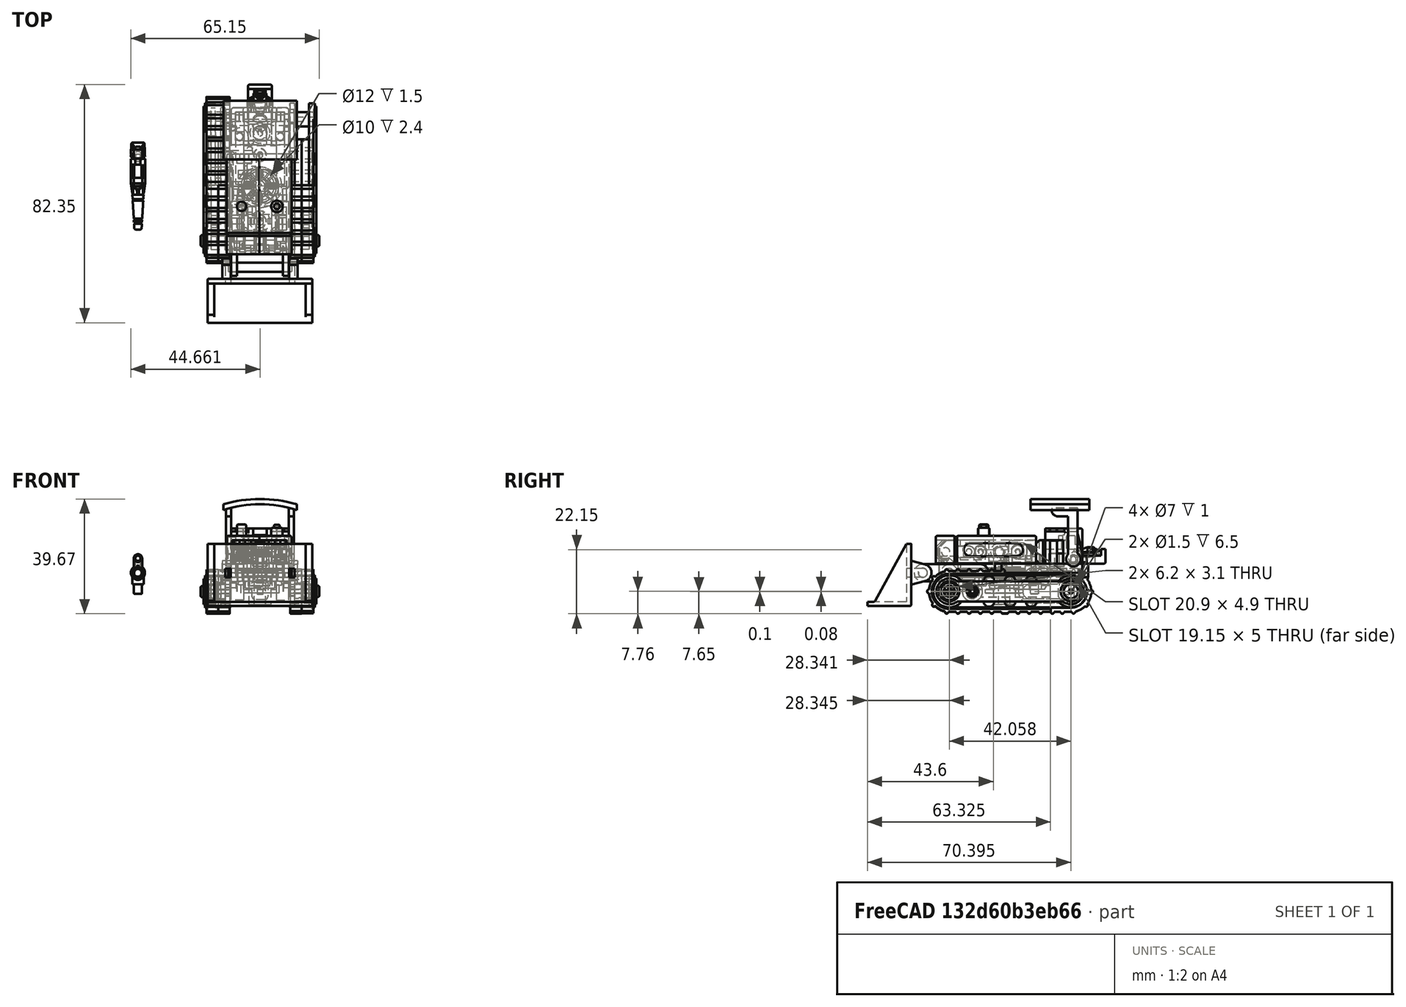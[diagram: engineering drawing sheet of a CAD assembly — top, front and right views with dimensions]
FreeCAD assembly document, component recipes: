
FREECAD ASSEMBLY — COMPONENT RECIPES ("Bonecrusher")

This assembly document has 22 components, labeled P0..P21 below (a component is one placed body or linked part). 22 of them carry a construction recipe — the FreeCAD feature program that regenerates the part from scratch, quoted from this document or its linked companion documents; the rest are supplied as boundary geometry only. No exploded tour is included for this assembly.
NOTE — document 2 of 4 of this assembly tour. The two overview renders and the header above are repeated from document 1; the component sections below continue where the previous document stopped.
COMPONENT P5 — recipe-attached ("L_Arm_Shield", modeled in this document).
Construction recipe (the document's own serialized feature program — sketch geometry with constraints, then the solid features built on it; lengths are millimeters unless a unit is written):

FEATURE [Sketcher::SketchObject] Sketch164
  ArcFitTolerance = 1e-06
  AttachmentSupport = -> [XY_Plane016]
  FullyConstrained = true
  MakeInternals = false
  MapMode = 5
  sketch-geometry (4):
    g0: LineSegment StartX=-34.7 StartY=4.75 StartZ=0 EndX=-34.7 EndY=-4.75 EndZ=0
    g1: LineSegment StartX=-34.7 StartY=-4.75 StartZ=0 EndX=0 EndY=-4.75 EndZ=0
    g2: LineSegment StartX=0 StartY=-4.75 StartZ=0 EndX=0 EndY=4.75 EndZ=0
    g3: LineSegment StartX=0 StartY=4.75 StartZ=0 EndX=-34.7 EndY=4.75 EndZ=0
  constraints (12):
    c: Coincident(g0,g1)
    c: Coincident(g1,g2)
    c: Coincident(g2,g3)
    c: Coincident(g3,g0)
    c: Vertical(g0)
    c: Vertical(g2)
    c: Horizontal(g1)
    c: Horizontal(g3)
    c: PointOnObject(g1,g-2)
    c: DistanceX(g3,g3) = 34.7
    c: DistanceY(g0,g0) = 9.5
    c: DistanceY(g-1,g2) = 4.75
FEATURE [PartDesign::Pad] Pad087
  Direction = (0,0,1)
  Length = 10.2
  Length2 = 10
  Profile = -> Sketch164
  ReferenceAxis = -> Sketch164 [N_Axis]
  Refine = true
  Suppressed = false
  Type = 0
FEATURE [Sketcher::SketchObject] Sketch165
  ArcFitTolerance = 1e-06
  AttachmentSupport = -> [Pad087]
  ExternalGeometry = -> [Pad087]
  FullyConstrained = true
  MakeInternals = false
  MapMode = 5
  Placement = pos=(0,0,10.2) rot=(0,0,1;0rad)
  sketch-geometry (4):
    g0: LineSegment StartX=-34.7 StartY=4.75 StartZ=0 EndX=-34.7 EndY=-3.25 EndZ=0
    g1: LineSegment StartX=-34.7 StartY=-3.25 StartZ=0 EndX=0 EndY=-3.25 EndZ=0
    g2: LineSegment StartX=0 StartY=-3.25 StartZ=0 EndX=0 EndY=4.75 EndZ=0
    g3: LineSegment StartX=0 StartY=4.75 StartZ=0 EndX=-34.7 EndY=4.75 EndZ=0
  constraints (11):
    c: Coincident(g0,g1)
    c: Coincident(g1,g2)
    c: Coincident(g2,g3)
    c: Coincident(g3,g0)
    c: Vertical(g0)
    c: Vertical(g2)
    c: Horizontal(g1)
    c: Horizontal(g3)
    c: Coincident(g0,g-3)
    c: PointOnObject(g1,g-4)
    c: DistanceY(g2,g2) = 8
FEATURE [PartDesign::Pocket] Pocket082
  BaseFeature = -> Pad087
  Direction = (0,0,-1)
  Length = 8.4
  Length2 = 5
  Profile = -> Sketch165
  ReferenceAxis = -> Sketch165 [N_Axis]
  Refine = true
  Suppressed = false
  Type = 0
FEATURE [Sketcher::SketchObject] Sketch166
  ArcFitTolerance = 1e-06
  AttachmentSupport = -> [Pocket082]
  ExternalGeometry = -> [Pocket082]
  FullyConstrained = true
  MakeInternals = false
  MapMode = 5
  Placement = pos=(0,0,1.8) rot=(0,0,1;0rad)
  sketch-geometry (4):
    g0: LineSegment StartX=-18.4 StartY=4.75 StartZ=0 EndX=-18.4 EndY=-3.25 EndZ=0
    g1: LineSegment StartX=-18.4 StartY=-3.25 StartZ=0 EndX=-7.1 EndY=-3.25 EndZ=0
    g2: LineSegment StartX=-7.1 StartY=-3.25 StartZ=0 EndX=-7.1 EndY=4.75 EndZ=0
    g3: LineSegment StartX=-7.1 StartY=4.75 StartZ=0 EndX=-18.4 EndY=4.75 EndZ=0
  constraints (12):
    c: Coincident(g0,g1)
    c: Coincident(g1,g2)
    c: Coincident(g2,g3)
    c: Coincident(g3,g0)
    c: Vertical(g0)
    c: Vertical(g2)
    c: Horizontal(g1)
    c: Horizontal(g3)
    c: DistanceX(g1,g-1) = 7.1
    c: DistanceX(g3,g3) = 11.3
    c: PointOnObject(g2,g-3)
    c: PointOnObject(g1,g-4)
FEATURE [PartDesign::Pad] Pad088
  BaseFeature = -> Pocket082
  Direction = (0,0,1)
  Length = 3.8
  Length2 = 10
  Profile = -> Sketch166
  ReferenceAxis = -> Sketch166 [N_Axis]
  Refine = true
  Suppressed = false
  Type = 0
FEATURE [Sketcher::SketchObject] Sketch167
  ArcFitTolerance = 1e-06
  AttachmentSupport = -> [Pad088]
  ExternalGeometry = -> [Pad088]
  FullyConstrained = true
  MakeInternals = false
  MapMode = 5
  Placement = pos=(0,0,1.8) rot=(0,0,1;0rad)
  sketch-geometry (1):
    g0: Circle CenterX=-22 CenterY=0.75 CenterZ=0 NormalX=0 NormalY=0 NormalZ=1 AngleXU=0 Radius=1.5
  constraints (3):
    c: Diameter(g0) = 3
    c: DistanceX(g-3,g0) = 12.7
    c: DistanceY(g0,g-3) = 4
FEATURE [PartDesign::Pad] Pad089
  BaseFeature = -> Pad088
  Direction = (0,0,1)
  Length = 7.5
  Length2 = 10
  Profile = -> Sketch167
  ReferenceAxis = -> Sketch167 [N_Axis]
  Refine = true
  Suppressed = false
  Type = 0
FEATURE [PartDesign::Fillet] Fillet035
  Base = -> Pad089 [Edge7,Edge2,Edge1,Edge10,Edge8]
  BaseFeature = -> Pad089
  Radius = 0.5
  Refine = true
  SupportTransform = false
  Suppressed = false
  UseAllEdges = false
FEATURE [Sketcher::SketchObject] Sketch168
  ArcFitTolerance = 1e-06
  AttachmentSupport = -> [Fillet035]
  ExternalGeometry = -> [Fillet035]
  FullyConstrained = true
  MakeInternals = false
  MapMode = 5
  Placement = pos=(0,0,5.6) rot=(0,0,1;0rad)
  sketch-geometry (4):
    g0: LineSegment StartX=-17.15 StartY=3.5 StartZ=0 EndX=-17.15 EndY=-3.25 EndZ=0
    g1: LineSegment StartX=-17.15 StartY=-3.25 StartZ=0 EndX=-8.35 EndY=-3.25 EndZ=0
    g2: LineSegment StartX=-8.35 StartY=-3.25 StartZ=0 EndX=-8.35 EndY=3.5 EndZ=0
    g3: LineSegment StartX=-8.35 StartY=3.5 StartZ=0 EndX=-17.15 EndY=3.5 EndZ=0
  constraints (12):
    c: Coincident(g0,g1)
    c: Coincident(g1,g2)
    c: Coincident(g2,g3)
    c: Coincident(g3,g0)
    c: Vertical(g0)
    c: Vertical(g2)
    c: Horizontal(g1)
    c: Horizontal(g3)
    c: DistanceY(g0,g-3) = 1.25
    c: PointOnObject(g0,g-4)
    c: DistanceX(g2,g-3) = 1.25
    c: DistanceX(g-3,g0) = 1.25
FEATURE [PartDesign::Pocket] Pocket083
  BaseFeature = -> Fillet035
  Direction = (0,0,-1)
  Length = 3.81
  Length2 = 5
  Profile = -> Sketch168
  ReferenceAxis = -> Sketch168 [N_Axis]
  Refine = true
  Suppressed = false
  Type = 0
FEATURE [Sketcher::SketchObject] Sketch169
  ArcFitTolerance = 1e-06
  AttachmentSupport = -> [Pocket083]
  ExternalGeometry = -> [Pocket083]
  FullyConstrained = false
  MakeInternals = false
  MapMode = 5
  Placement = pos=(0,0,1.79) rot=(0,0,1;0rad)
  sketch-geometry (4):
    g0: LineSegment StartX=-8.35 StartY=2.75 StartZ=0 EndX=-11.5 EndY=2.75 EndZ=0
    g1: ArcOfCircle CenterX=-11.5 CenterY=0.75 CenterZ=0 NormalX=0 NormalY=0 NormalZ=1 AngleXU=0 Radius=2 StartAngle=1.5708 EndAngle=4.71238
    g2: LineSegment StartX=-11.5 StartY=-1.25 StartZ=0 EndX=-8.35 EndY=-1.25 EndZ=0
    g3: LineSegment StartX=-8.35 StartY=-1.25 StartZ=0 EndX=-8.35 EndY=2.75 EndZ=0
  constraints (12):
    c: Horizontal(g0)
    c: Coincident(g1,g0)
    c: Coincident(g2,g1)
    c: Horizontal(g2)
    c: Coincident(g3,g2)
    c: Coincident(g3,g0)
    c: Vertical(g3)
    c: PointOnObject(g0,g-3)
    c: DistanceY(g2,g0) = 4
    c: DistanceY(g0,g-4) = 2
    c: Diameter(g1) = 4
    c: DistanceX(g0,g0) = 3.15
FEATURE [Sketcher::SketchObject] Sketch170
  ArcFitTolerance = 1e-06
  AttachmentSupport = -> [Pocket083]
  ExternalGeometry = -> [Pocket083]
  FullyConstrained = true
  MakeInternals = false
  MapMode = 5
  Placement = pos=(0,0,5.6) rot=(0,0,1;0rad)
  sketch-geometry (4):
    g0: LineSegment StartX=-8.35 StartY=2.75 StartZ=0 EndX=-8.35 EndY=-1.25 EndZ=0
    g1: LineSegment StartX=-8.35 StartY=-1.25 StartZ=0 EndX=-7.1 EndY=-1.25 EndZ=0
    g2: LineSegment StartX=-7.1 StartY=-1.25 StartZ=0 EndX=-7.1 EndY=2.75 EndZ=0
    g3: LineSegment StartX=-7.1 StartY=2.75 StartZ=0 EndX=-8.35 EndY=2.75 EndZ=0
  constraints (12):
    c: Coincident(g0,g1)
    c: Coincident(g1,g2)
    c: Coincident(g2,g3)
    c: Coincident(g3,g0)
    c: Vertical(g0)
    c: Vertical(g2)
    c: Horizontal(g1)
    c: Horizontal(g3)
    c: DistanceY(g2,g-3) = 2
    c: PointOnObject(g0,g-4)
    c: PointOnObject(g2,g-5)
    c: DistanceY(g1,g2) = 4
FEATURE [PartDesign::Pocket] Pocket084
  BaseFeature = -> Pocket083
  Direction = (0,0,-1)
  Length = 1.25
  Length2 = 5
  Profile = -> Sketch170
  ReferenceAxis = -> Sketch170 [N_Axis]
  Refine = true
  Suppressed = false
  Type = 0
FEATURE [PartDesign::Pad] Pad090
  BaseFeature = -> Pocket084
  Direction = (0,0,1)
  Length = 2.56
  Length2 = 10
  Profile = -> Sketch169
  ReferenceAxis = -> Sketch169 [N_Axis]
  Refine = true
  Suppressed = false
  Type = 0
FEATURE [Sketcher::SketchObject] Sketch171
  ArcFitTolerance = 1e-06
  AttachmentSupport = -> [Pad090]
  ExternalGeometry = -> [Pad090]
  FullyConstrained = true
  MakeInternals = false
  MapMode = 5
  Placement = pos=(0,0,1.79) rot=(0,0,1;0rad)
  sketch-geometry (1):
    g0: Circle CenterX=-15.5 CenterY=0.75 CenterZ=0 NormalX=0 NormalY=0 NormalZ=1 AngleXU=0 Radius=1.9
  constraints (3):
    c: DistanceY(g0,g-3) = 4
    c: Diameter(g0) = 3.8
    c: DistanceX(g-5,g0) = 1.65
FEATURE [PartDesign::Pad] Pad091
  BaseFeature = -> Pad090
  Direction = (0,0,1)
  Length = 5
  Length2 = 10
  Profile = -> Sketch171
  ReferenceAxis = -> Sketch171 [N_Axis]
  Refine = true
  Suppressed = false
  Type = 0
FEATURE [Sketcher::SketchObject] Sketch172
  ArcFitTolerance = 1e-06
  AttachmentSupport = -> [Pad091]
  ExternalGeometry = -> [Pad091]
  FullyConstrained = true
  MakeInternals = false
  MapMode = 5
  Placement = pos=(0,0,4.35) rot=(0,0,1;0rad)
  sketch-geometry (1):
    g0: Circle CenterX=-11.5 CenterY=0.75 CenterZ=0 NormalX=0 NormalY=0 NormalZ=1 AngleXU=0 Radius=1.05
  constraints (3):
    c: DistanceY(g0,g-4) = 2
    c: DistanceX(g0,g-3) = 4.4
    c: Diameter(g0) = 2.1
FEATURE [PartDesign::Pocket] Pocket085
  BaseFeature = -> Pad091
  Direction = (0,0,-1)
  Length = 2.56
  Length2 = 5
  Profile = -> Sketch172
  ReferenceAxis = -> Sketch172 [N_Axis]
  Refine = true
  Suppressed = false
  Type = 0
FEATURE [Sketcher::SketchObject] Sketch173
  ArcFitTolerance = 1e-06
  AttachmentSupport = -> [Pocket085]
  ExternalGeometry = -> [Pocket085]
  FullyConstrained = true
  MakeInternals = false
  MapMode = 5
  Placement = pos=(0,0,6.79) rot=(0,0,1;0rad)
  sketch-geometry (1):
    g0: Circle CenterX=-15.5 CenterY=0.75 CenterZ=0 NormalX=0 NormalY=0 NormalZ=1 AngleXU=0 Radius=0.75
  constraints (2):
    c: Diameter(g0) = 1.5
    c: Coincident(g0,g-3)
FEATURE [PartDesign::Pocket] Pocket086
  BaseFeature = -> Pocket085
  Direction = (0,0,-1)
  Length = 5
  Length2 = 5
  Profile = -> Sketch173
  ReferenceAxis = -> Sketch173 [N_Axis]
  Refine = true
  Suppressed = false
  Type = 0
FEATURE [Sketcher::SketchObject] Sketch174
  ArcFitTolerance = 1e-06
  AttachmentSupport = -> [Pocket086]
  ExternalGeometry = -> [Pocket086]
  FullyConstrained = true
  MakeInternals = false
  MapMode = 5
  Placement = pos=(0,0,0) rot=(1,0,0;3.14159rad)
  sketch-geometry (8):
    g0: ArcOfCircle CenterX=-27.95 CenterY=0 CenterZ=0 NormalX=0 NormalY=0 NormalZ=1 AngleXU=0 Radius=2.25 StartAngle=1.5708 EndAngle=4.71239
    g1: ArcOfCircle CenterX=-11.95 CenterY=1e-16 CenterZ=0 NormalX=0 NormalY=0 NormalZ=1 AngleXU=0 Radius=2.25 StartAngle=4.71239 EndAngle=7.85398
    g2: LineSegment StartX=-27.95 StartY=2.25 StartZ=0 EndX=-11.95 EndY=2.25 EndZ=0
    g3: LineSegment StartX=-27.95 StartY=-2.25 StartZ=0 EndX=-11.95 EndY=-2.25 EndZ=0
    g4: LineSegment StartX=-7.45 StartY=4.75 StartZ=0 EndX=-7.45 EndY=-4.75 EndZ=0
    g5: LineSegment StartX=-7.45 StartY=-4.75 StartZ=0 EndX=-6.45 EndY=-4.75 EndZ=0
    g6: LineSegment StartX=-6.45 StartY=-4.75 StartZ=0 EndX=-6.45 EndY=4.75 EndZ=0
    g7: LineSegment StartX=-6.45 StartY=4.75 StartZ=0 EndX=-7.45 EndY=4.75 EndZ=0
  constraints (22):
    c: Tangent(g0,g2) = 1.5708
    c: Tangent(g0,g3) = -1.5708
    c: Tangent(g1,g2) = 1.5708
    c: Tangent(g1,g3) = -1.5708
    c: Equal(g0,g1)
    c: Horizontal(g3)
    c: PointOnObject(g0,g-1)
    c: Diameter(g0) = 4.5
    c: DistanceX(g-3,g0) = 6.75
    c: DistanceX(g0,g1) = 16
    c: Coincident(g4,g5)
    c: Coincident(g5,g6)
    c: Coincident(g6,g7)
    c: Coincident(g7,g4)
    c: Vertical(g4)
    c: Vertical(g6)
    c: Horizontal(g5)
    c: Horizontal(g7)
    c: PointOnObject(g6,g-4)
    c: PointOnObject(g5,g-5)
    c: DistanceX(g1,g4) = 4.5
    c: DistanceX(g4,g6) = 1
FEATURE [PartDesign::Pocket] Pocket087
  BaseFeature = -> Pocket086
  Direction = (0,0,1)
  Length = 0.3
  Length2 = 5
  Profile = -> Sketch174
  ReferenceAxis = -> Sketch174 [N_Axis]
  Refine = true
  Suppressed = false
  Type = 0
FEATURE [Sketcher::SketchObject] Sketch175
  ArcFitTolerance = 1e-06
  AttachmentSupport = -> [Pocket087]
  ExternalGeometry = -> [Pocket087]
  FullyConstrained = true
  MakeInternals = false
  MapMode = 5
  Placement = pos=(0,-4.75,0) rot=(1,0,0;1.5708rad)
  sketch-geometry (4):
    g0: LineSegment StartX=-7.45 StartY=10.2 StartZ=0 EndX=-7.45 EndY=0 EndZ=0
    g1: LineSegment StartX=-7.45 StartY=0 StartZ=0 EndX=-6.45 EndY=0 EndZ=0
    g2: LineSegment StartX=-6.45 StartY=0 StartZ=0 EndX=-6.45 EndY=10.2 EndZ=0
    g3: LineSegment StartX=-6.45 StartY=10.2 StartZ=0 EndX=-7.45 EndY=10.2 EndZ=0
  constraints (11):
    c: Coincident(g0,g1)
    c: Coincident(g1,g2)
    c: Coincident(g2,g3)
    c: Coincident(g3,g0)
    c: Vertical(g0)
    c: Vertical(g2)
    c: Horizontal(g1)
    c: Horizontal(g3)
    c: DistanceX(g3,g3) = 1
    c: Coincident(g0,g-3)
    c: PointOnObject(g0,g-4)
FEATURE [PartDesign::Pocket] Pocket088
  BaseFeature = -> Pocket087
  Direction = (0,1,-2e-16)
  Length = 0.3
  Length2 = 5
  Profile = -> Sketch175
  ReferenceAxis = -> Sketch175 [N_Axis]
  Refine = true
  Suppressed = false
  Type = 0
FEATURE [PartDesign::Fillet] Fillet036
  Base = -> Pocket088 [Edge90,Edge91,Edge89,Edge92]
  BaseFeature = -> Pocket088
  Radius = 0.2
  Refine = true
  SupportTransform = false
  Suppressed = false
  UseAllEdges = false
FEATURE [PartDesign::Fillet] Fillet037
  Base = -> Fillet036 [Edge5,Edge94,Edge20,Edge19,Edge18,Edge17,Edge93,Edge97,Edge96,Edge95]
  BaseFeature = -> Fillet036
  Radius = 0.2
  Refine = true
  SupportTransform = false
  Suppressed = false
  UseAllEdges = false
FEATURE [Sketcher::SketchObject] Sketch176
  ArcFitTolerance = 1e-06
  AttachmentSupport = -> [Fillet037]
  ExternalGeometry = -> [Fillet037]
  FullyConstrained = true
  MakeInternals = false
  MapMode = 5
  Placement = pos=(0,-4.75,0) rot=(1,0,0;1.5708rad)
  sketch-geometry (1):
    g0: Circle CenterX=-16.6 CenterY=5.1 CenterZ=0 NormalX=0 NormalY=0 NormalZ=1 AngleXU=0 Radius=2
  constraints (3):
    c: Diameter(g0) = 4
    c: DistanceY(g0,g-3) = 5.1
    c: DistanceX(g0,g-4) = 16.6
FEATURE [PartDesign::Pad] Pad092
  BaseFeature = -> Fillet037
  Direction = (0,-1,2e-16)
  Length = 2.8
  Length2 = 10
  Profile = -> Sketch176
  ReferenceAxis = -> Sketch176 [N_Axis]
  Refine = true
  Suppressed = false
  Type = 0
FEATURE [PartDesign::Fillet] Fillet038
  Base = -> Pad092 [Edge116]
  BaseFeature = -> Pad092
  Radius = 0.5
  Refine = true
  SupportTransform = false
  Suppressed = false
  UseAllEdges = false
FEATURE [PartDesign::Fillet] Fillet039
  Base = -> Fillet038 [Edge89,Edge85]
  BaseFeature = -> Fillet038
  Radius = 0.5
  Refine = true
  SupportTransform = false
  Suppressed = false
  UseAllEdges = false
FEATURE [Sketcher::SketchObject] Sketch178
  ArcFitTolerance = 1e-06
  AttachmentSupport = -> [Fillet039]
  ExternalGeometry = -> [Fillet039]
  FullyConstrained = true
  MakeInternals = false
  MapMode = 5
  Placement = pos=(0,-7.55,2e-15) rot=(1,0,0;1.5708rad)
  sketch-geometry (1):
    g0: Circle CenterX=-16.6 CenterY=5.1 CenterZ=0 NormalX=0 NormalY=0 NormalZ=1 AngleXU=0 Radius=1
  constraints (2):
    c: Coincident(g0,g-3)
    c: Diameter(g0) = 2
FEATURE [PartDesign::Pad] Pad093
  BaseFeature = -> Fillet039
  Direction = (0,-1,2e-16)
  Length = 1.1
  Length2 = 10
  Profile = -> Sketch178
  ReferenceAxis = -> Sketch178 [N_Axis]
  Refine = true
  Suppressed = false
  Type = 0
FEATURE [PartDesign::Fillet] Fillet040
  Base = -> Pad093 [Edge182]
  BaseFeature = -> Pad093
  Radius = 0.5
  Refine = true
  SupportTransform = false
  Suppressed = false
  UseAllEdges = false
FEATURE [Sketcher::SketchObject] Sketch283
  ArcFitTolerance = 1e-06
  AttachmentSupport = -> [Fillet040]
  ExternalGeometry = -> [Fillet040]
  FullyConstrained = true
  MakeInternals = false
  MapMode = 5
  Placement = pos=(0,0,10.2) rot=(0,0,1;0rad)
  sketch-geometry (12):
    g0: LineSegment StartX=0 StartY=-3.25 StartZ=0 EndX=1e-16 EndY=-4.25 EndZ=0
    g1: LineSegment StartX=-0.5 StartY=-4.75 StartZ=0 EndX=-6.25 EndY=-4.75 EndZ=0
    g2: ArcOfCircle CenterX=-6.25 CenterY=-4.55 CenterZ=0 NormalX=0 NormalY=0 NormalZ=1 AngleXU=0 Radius=0.2 StartAngle=3.14159 EndAngle=4.71239
    g3: LineSegment StartX=-6.45 StartY=-4.55 StartZ=0 EndX=-6.45 EndY=-4.45 EndZ=0
    g4: LineSegment StartX=-6.45 StartY=-4.45 StartZ=0 EndX=-7.45 EndY=-4.45 EndZ=0
    g5: LineSegment StartX=-7.45 StartY=-4.45 StartZ=0 EndX=-7.45 EndY=-4.55 EndZ=0
    g6: ArcOfCircle CenterX=-7.65 CenterY=-4.55 CenterZ=0 NormalX=0 NormalY=0 NormalZ=1 AngleXU=0 Radius=0.2 StartAngle=4.71239 EndAngle=6.28319
    g7: LineSegment StartX=-7.65 StartY=-4.75 StartZ=0 EndX=-34.2 EndY=-4.75 EndZ=0
    g8: ArcOfCircle CenterX=-34.2 CenterY=-4.25 CenterZ=0 NormalX=0 NormalY=0 NormalZ=1 AngleXU=0 Radius=0.5 StartAngle=3.14159 EndAngle=4.71239
    g9: LineSegment StartX=-34.7 StartY=-4.25 StartZ=0 EndX=-34.7 EndY=-3.25 EndZ=0
    g10: LineSegment StartX=-34.7 StartY=-3.25 StartZ=0 EndX=0 EndY=-3.25 EndZ=0
    g11: ArcOfCircle CenterX=-0.5 CenterY=-4.25 CenterZ=0 NormalX=0 NormalY=0 NormalZ=1 AngleXU=0 Radius=0.5 StartAngle=4.71239 EndAngle=6.28319
  constraints (28):
    c: Coincident(g2,g-9)
    c: Coincident(g2,g1)
    c: Coincident(g4,g3)
    c: Coincident(g4,g-10)
    c: Coincident(g5,g4)
    c: Coincident(g5,g-11)
    c: Coincident(g6,g5)
    c: Coincident(g6,g-12)
    c: Coincident(g8,g7)
    c: Coincident(g8,g-14)
    c: Coincident(g10,g9)
    c: Coincident(g10,g0)
    c: Coincident(g0,g-5)
    c: Coincident(g1,g-6)
    c: Coincident(g0,g-4)
    c: Coincident(g1,g-7)
    c: Coincident(g3,g2)
    c: Radius(g2) = 0.2
    c: Coincident(g3,g-9)
    c: Coincident(g11,g0)
    c: Coincident(g11,g1)
    c: Radius(g11) = 0.5
    c: Coincident(g7,g6)
    c: Radius(g6) = 0.2
    c: Coincident(g9,g8)
    c: Coincident(g-13,g7)
    c: Radius(g8) = 0.5
    c: Coincident(g9,g-14)
FEATURE [PartDesign::Pad] Pad162
  BaseFeature = -> Fillet040
  Direction = (0,0,1)
  Length = 1
  Length2 = 10
  Profile = -> Sketch283
  ReferenceAxis = -> Sketch283 [N_Axis]
  Refine = true
  Suppressed = false
  Type = 0
FEATURE [PartDesign::Body] Body014  label="L_Arm_Shield"
  AllowCompound = false
  Group = -> [Sketch164,Pad087,Sketch165,Pocket082,Sketch166,Pad088,Sketch167,Pad089,Fillet035,Sketch168,Pocket083,Sketch169,Sketch170,Pocket084,Pad090,Sketch171,Pad091,Sketch172,Pocket085,Sketch173,Pocket086,Sketch174,Pocket087,Sketch175,Pocket088,Fillet036,Fillet037,Sketch176,Pad092,Fillet038,Fillet039,Sketch178,Pad093,Fillet040,Sketch283,Pad162]
  Origin = -> Origin016
  Tip = -> Pad162
COMPONENT P6 — recipe-attached ("Right_Inner_Leg", modeled in this document).
Construction recipe (the document's own serialized feature program — sketch geometry with constraints, then the solid features built on it; lengths are millimeters unless a unit is written):

FEATURE [Sketcher::SketchObject] Sketch187
  ArcFitTolerance = 1e-06
  AttachmentSupport = -> [XY_Plane017]
  FullyConstrained = true
  MakeInternals = false
  MapMode = 5
  sketch-geometry (4):
    g0: LineSegment StartX=3e-16 StartY=5.55 StartZ=0 EndX=42.05 EndY=5.55 EndZ=0
    g1: ArcOfCircle CenterX=42.05 CenterY=3.35631e-11 CenterZ=0 NormalX=0 NormalY=0 NormalZ=1 AngleXU=0 Radius=5.55 StartAngle=4.71239 EndAngle=7.85398
    g2: LineSegment StartX=42.05 StartY=-5.55 StartZ=0 EndX=0 EndY=-5.55 EndZ=0
    g3: ArcOfCircle CenterX=0 CenterY=0 CenterZ=0 NormalX=0 NormalY=0 NormalZ=1 AngleXU=0 Radius=5.55 StartAngle=1.5708 EndAngle=4.71239
  constraints (13):
    c: PointOnObject(g0,g-2)
    c: Horizontal(g0)
    c: Coincident(g1,g0)
    c: Coincident(g2,g1)
    c: PointOnObject(g2,g-2)
    c: Horizontal(g2)
    c: Coincident(g3,g2)
    c: Coincident(g3,g0)
    c: DistanceX(g0,g0) = 42.05
    c: Radius(g3) = 5.55
    c: Radius(g1) = 5.55
    c: Coincident(g3,g-1)
    c: PointOnObject(g1,g-1)
FEATURE [PartDesign::Pad] Pad098
  Direction = (0,0,1)
  Length = 1.6
  Length2 = 10
  Profile = -> Sketch187
  ReferenceAxis = -> Sketch187 [N_Axis]
  Refine = true
  Suppressed = false
  Type = 0
FEATURE [Sketcher::SketchObject] Sketch188
  ArcFitTolerance = 1e-06
  AttachmentSupport = -> [Pad098]
  ExternalGeometry = -> [Pad098]
  FullyConstrained = true
  MakeInternals = false
  MapMode = 5
  Placement = pos=(0,0,0) rot=(1,0,0;3.14159rad)
  sketch-geometry (8):
    g0: LineSegment StartX=19.17 StartY=5.55 StartZ=0 EndX=0 EndY=5.55 EndZ=0
    g1: ArcOfCircle CenterX=0 CenterY=1e-16 CenterZ=0 NormalX=0 NormalY=0 NormalZ=1 AngleXU=0 Radius=5.55 StartAngle=1.5708 EndAngle=4.71239
    g2: LineSegment StartX=-1e-15 StartY=-5.55 StartZ=0 EndX=35.05 EndY=-5.55 EndZ=0
    g3: LineSegment StartX=19.17 StartY=5.55 StartZ=0 EndX=19.17 EndY=7.05 EndZ=0
    g4: LineSegment StartX=19.17 StartY=7.05 StartZ=0 EndX=0 EndY=7.05 EndZ=0
    g5: ArcOfCircle CenterX=0 CenterY=1e-16 CenterZ=0 NormalX=0 NormalY=0 NormalZ=1 AngleXU=0 Radius=7.05 StartAngle=1.5708 EndAngle=4.71239
    g6: LineSegment StartX=0 StartY=-7.05 StartZ=0 EndX=35.05 EndY=-7.05 EndZ=0
    g7: LineSegment StartX=35.05 StartY=-5.55 StartZ=0 EndX=35.05 EndY=-7.05 EndZ=0
  constraints (24):
    c: Coincident(g0,g-4)
    c: Coincident(g1,g0)
    c: Coincident(g1,g-5)
    c: Coincident(g2,g1)
    c: PointOnObject(g2,g-5)
    c: PointOnObject(g0,g-3)
    c: DistanceX(g2,g2) = 35.05
    c: DistanceX(g0,g0) = 19.17
    c: Coincident(g1,g-1)
    c: Coincident(g3,g0)
    c: Vertical(g3)
    c: Coincident(g4,g3)
    c: PointOnObject(g4,g-2)
    c: Horizontal(g4)
    c: Coincident(g5,g4)
    c: PointOnObject(g5,g-2)
    c: Coincident(g6,g5)
    c: Horizontal(g6)
    c: Coincident(g7,g2)
    c: Coincident(g7,g6)
    c: Vertical(g7)
    c: DistanceY(g3,g3) = 1.5
    c: DistanceY(g7,g7) = 1.5
    c: Coincident(g5,g1)
FEATURE [PartDesign::Pad] Pad099
  BaseFeature = -> Pad098
  Direction = (0,0,-1)
  Length = 4.05
  Length2 = 10
  Profile = -> Sketch188
  ReferenceAxis = -> Sketch188 [N_Axis]
  Refine = true
  Reversed = true
  Suppressed = false
  Type = 0
FEATURE [PartDesign::Pocket] Pocket093
  BaseFeature = -> Pad099
  Direction = (0,0,1)
  Length = 0.1
  Length2 = 5
  Profile = -> Sketch188
  ReferenceAxis = -> Sketch188 [N_Axis]
  Refine = true
  Suppressed = false
  Type = 0
FEATURE [Sketcher::SketchObject] Sketch189
  ArcFitTolerance = 1e-06
  AttachmentSupport = -> [Pocket093]
  FullyConstrained = true
  MakeInternals = false
  MapMode = 5
  Placement = pos=(0,0,0) rot=(1,0,0;3.14159rad)
  sketch-geometry (5):
    g0: LineSegment StartX=-3 StartY=1.5 StartZ=0 EndX=-3 EndY=-1.5 EndZ=0
    g1: LineSegment StartX=-3 StartY=-1.5 StartZ=0 EndX=3 EndY=-1.5 EndZ=0
    g2: LineSegment StartX=3 StartY=-1.5 StartZ=0 EndX=3 EndY=1.5 EndZ=0
    g3: LineSegment StartX=3 StartY=1.5 StartZ=0 EndX=-3 EndY=1.5 EndZ=0
    g4: Circle CenterX=8 CenterY=0 CenterZ=0 NormalX=0 NormalY=0 NormalZ=1 AngleXU=0 Radius=0.75
  constraints (15):
    c: Coincident(g0,g1)
    c: Coincident(g1,g2)
    c: Coincident(g2,g3)
    c: Coincident(g3,g0)
    c: Vertical(g0)
    c: Vertical(g2)
    c: Horizontal(g1)
    c: Horizontal(g3)
    c: DistanceY(g-1,g0) = 1.5
    c: DistanceY(g0,g-1) = 1.5
    c: DistanceX(g0,g-1) = 3
    c: DistanceX(g-1,g2) = 3
    c: PointOnObject(g4,g-1)
    c: Diameter(g4) = 1.5
    c: DistanceX(g-1,g4) = 8
FEATURE [PartDesign::Pocket] Pocket094
  BaseFeature = -> Pocket093
  Direction = (0,0,1)
  Length = 1.6
  Length2 = 5
  Profile = -> Sketch189
  ReferenceAxis = -> Sketch189 [N_Axis]
  Refine = true
  Suppressed = false
  Type = 0
FEATURE [Sketcher::SketchObject] Sketch190
  ArcFitTolerance = 1e-06
  AttachmentSupport = -> [Pocket094]
  ExternalGeometry = -> [Pocket094]
  FullyConstrained = true
  MakeInternals = false
  MapMode = 5
  Placement = pos=(0,0,0.1) rot=(1,0,0;3.14159rad)
  sketch-geometry (38):
    g0: ArcOfCircle CenterX=18.57 CenterY=7.05 CenterZ=0 NormalX=0 NormalY=0 NormalZ=1 AngleXU=0 Radius=0.6 StartAngle=-4.4e-15 EndAngle=3.14159
    g1: ArcOfCircle CenterX=14.67 CenterY=7.05 CenterZ=0 NormalX=0 NormalY=0 NormalZ=1 AngleXU=0 Radius=0.6 StartAngle=-8e-15 EndAngle=3.14159
    g2: ArcOfCircle CenterX=10.77 CenterY=7.05 CenterZ=0 NormalX=0 NormalY=0 NormalZ=1 AngleXU=0 Radius=0.6 StartAngle=6e-16 EndAngle=3.14159
    g3: ArcOfCircle CenterX=6.87 CenterY=7.05 CenterZ=0 NormalX=0 NormalY=0 NormalZ=1 AngleXU=0 Radius=0.6 StartAngle=-4.4e-15 EndAngle=3.14159
    g4: LineSegment StartX=19.17 StartY=7.05 StartZ=0 EndX=17.97 EndY=7.05 EndZ=0
    g5: LineSegment StartX=15.27 StartY=7.05 StartZ=0 EndX=14.07 EndY=7.05 EndZ=0
    g6: LineSegment StartX=11.37 StartY=7.05 StartZ=0 EndX=10.17 EndY=7.05 EndZ=0
    g7: LineSegment StartX=7.47 StartY=7.05 StartZ=0 EndX=6.27 EndY=7.05 EndZ=0
    g8: ArcOfCircle CenterX=2.97 CenterY=7.05 CenterZ=0 NormalX=0 NormalY=0 NormalZ=1 AngleXU=0 Radius=0.6 StartAngle=-1.8e-15 EndAngle=3.14159
    g9: LineSegment StartX=3.57 StartY=7.05 StartZ=0 EndX=2.37 EndY=7.05 EndZ=0
    g10: ArcOfCircle CenterX=-0.927604 CenterY=6.98871 CenterZ=0 NormalX=0 NormalY=0 NormalZ=1 AngleXU=0 Radius=0.6 StartAngle=0.0893917 EndAngle=3.31612
    g11: ArcOfCircle CenterX=-5.30424 CenterY=4.64408 CenterZ=0 NormalX=0 NormalY=0 NormalZ=1 AngleXU=0 Radius=0.6 StartAngle=0.809094 EndAngle=4.03582
    g12: ArcOfCircle CenterX=-7.05 CenterY=0 CenterZ=0 NormalX=0 NormalY=0 NormalZ=1 AngleXU=0 Radius=0.6 StartAngle=1.52823 EndAngle=4.75496
    g13: LineSegment StartX=-7.02447 StartY=0.599457 StartZ=0 EndX=-7.02447 EndY=-0.599457 EndZ=0
    g14: LineSegment StartX=-0.33 StartY=7.04227 StartZ=0 EndX=-1.51849 EndY=6.88453 EndZ=0
    g15: ArcOfCircle CenterX=-5.28202 CenterY=-4.63063 CenterZ=0 NormalX=0 NormalY=0 NormalZ=1 AngleXU=0 Radius=0.6 StartAngle=2.29058 EndAngle=5.43217
    g16: ArcOfCircle CenterX=-0.922566 CenterY=-6.98938 CenterZ=0 NormalX=0 NormalY=0 NormalZ=1 AngleXU=0 Radius=0.6 StartAngle=2.96779 EndAngle=6.19451
    g17: ArcOfCircle CenterX=2.97508 CenterY=-7.05 CenterZ=0 NormalX=0 NormalY=0 NormalZ=1 AngleXU=0 Radius=0.6 StartAngle=3.14159 EndAngle=6.28319
    g18: ArcOfCircle CenterX=6.87508 CenterY=-7.05 CenterZ=0 NormalX=0 NormalY=0 NormalZ=1 AngleXU=0 Radius=0.6 StartAngle=3.14159 EndAngle=6.28319
    g19: ArcOfCircle CenterX=10.7751 CenterY=-7.05 CenterZ=0 NormalX=0 NormalY=0 NormalZ=1 AngleXU=0 Radius=0.6 StartAngle=3.14159 EndAngle=6.28319
    g20: ArcOfCircle CenterX=14.6751 CenterY=-7.05 CenterZ=0 NormalX=0 NormalY=0 NormalZ=1 AngleXU=0 Radius=0.6 StartAngle=3.14159 EndAngle=6.28319
    g21: ArcOfCircle CenterX=23.7751 CenterY=-7.05 CenterZ=0 NormalX=0 NormalY=0 NormalZ=1 AngleXU=0 Radius=0.6 StartAngle=3.14159 EndAngle=6.28319
    g22: ArcOfCircle CenterX=27.6751 CenterY=-7.05 CenterZ=0 NormalX=0 NormalY=0 NormalZ=1 AngleXU=0 Radius=0.6 StartAngle=3.14159 EndAngle=6.28319
    g23: ArcOfCircle CenterX=31.5751 CenterY=-7.05 CenterZ=0 NormalX=0 NormalY=0 NormalZ=1 AngleXU=0 Radius=0.6 StartAngle=3.14159 EndAngle=6.28319
    g24: ArcOfCircle CenterX=18.5751 CenterY=-7.05 CenterZ=0 NormalX=0 NormalY=0 NormalZ=1 AngleXU=0 Radius=0.6 StartAngle=3.14159 EndAngle=4.71239
    g25: ArcOfCircle CenterX=19.8751 CenterY=-7.05 CenterZ=0 NormalX=0 NormalY=0 NormalZ=1 AngleXU=0 Radius=0.6 StartAngle=4.71239 EndAngle=6.28319
    g26: LineSegment StartX=19.8751 StartY=-7.65 StartZ=0 EndX=18.5751 EndY=-7.65 EndZ=0
    g27: LineSegment StartX=20.4751 StartY=-7.05 StartZ=0 EndX=17.9751 EndY=-7.05 EndZ=0
    g28: LineSegment StartX=24.3751 StartY=-7.05 StartZ=0 EndX=23.1751 EndY=-7.05 EndZ=0
    g29: LineSegment StartX=28.2751 StartY=-7.05 StartZ=0 EndX=27.0751 EndY=-7.05 EndZ=0
    g30: LineSegment StartX=32.1751 StartY=-7.05 StartZ=0 EndX=30.9751 EndY=-7.05 EndZ=0
    g31: LineSegment StartX=15.2751 StartY=-7.05 StartZ=0 EndX=14.0751 EndY=-7.05 EndZ=0
    g32: LineSegment StartX=11.3751 StartY=-7.05 StartZ=0 EndX=10.1751 EndY=-7.05 EndZ=0
    g33: LineSegment StartX=7.47508 StartY=-7.05 StartZ=0 EndX=6.27508 EndY=-7.05 EndZ=0
    g34: LineSegment StartX=3.57508 StartY=-7.05 StartZ=0 EndX=2.37508 EndY=-7.05 EndZ=0
    g35: LineSegment StartX=-0.324923 StartY=-7.04251 StartZ=0 EndX=-1.51353 EndY=-6.88562 EndZ=0
    g36: LineSegment StartX=-4.88649 StartY=-5.0818 StartZ=0 EndX=-5.67755 EndY=-4.17946 EndZ=0
    g37: LineSegment StartX=-4.89015 StartY=5.07828 StartZ=0 EndX=-5.67992 EndY=4.17625 EndZ=0
  constraints (132):
    c: Coincident(g4,g0)
    c: Coincident(g4,g0)
    c: Horizontal(g4)
    c: Coincident(g5,g1)
    c: Coincident(g5,g1)
    c: Horizontal(g5)
    c: Coincident(g6,g2)
    c: Coincident(g6,g2)
    c: Horizontal(g6)
    c: Coincident(g7,g3)
    c: Coincident(g7,g3)
    c: Horizontal(g7)
    c: Coincident(g9,g8)
    c: Coincident(g9,g8)
    c: Horizontal(g9)
    c: Radius(g0) = 0.6
    c: Radius(g1) = 0.6
    c: Radius(g2) = 0.6
    c: Radius(g3) = 0.6
    c: DistanceX(g3,g2) = 2.7
    c: Coincident(g0,g-3)
    c: PointOnObject(g0,g4)
    c: PointOnObject(g1,g-4)
    c: PointOnObject(g1,g5)
    c: DistanceX(g1,g0) = 2.7
    c: DistanceX(g2,g1) = 2.7
    c: DistanceX(g8,g3) = 2.7
    c: PointOnObject(g2,g6)
    c: PointOnObject(g2,g-4)
    c: PointOnObject(g3,g-4)
    c: PointOnObject(g3,g7)
    c: PointOnObject(g8,g-4)
    c: PointOnObject(g8,g9)
    c: Radius(g8) = 0.6
    c: PointOnObject(g10,g-5)
    c: PointOnObject(g10,g-5)
    c: PointOnObject(g11,g-5)
    c: PointOnObject(g11,g-5)
    c: PointOnObject(g12,g-5)
    c: PointOnObject(g12,g-5)
    c: PointOnObject(g12,g-1)
    c: PointOnObject(g12,g-5)
    c: Radius(g12) = 0.6
    c: Coincident(g13,g12)
    c: Coincident(g13,g12)
    c: Coincident(g14,g10)
    c: Coincident(g14,g10)
    c: PointOnObject(g15,g-5)
    c: PointOnObject(g15,g-5)
    c: PointOnObject(g16,g-5)
    c: PointOnObject(g16,g-5)
    c: Coincident(g26,g25)
    c: Coincident(g26,g24)
    c: Horizontal(g26)
    c: Coincident(g27,g25)
    c: Coincident(g27,g24)
    c: Horizontal(g27)
    c: Coincident(g28,g21)
    c: Coincident(g28,g21)
    c: Horizontal(g28)
    c: Coincident(g29,g22)
    c: Coincident(g29,g22)
    c: Horizontal(g29)
    c: Coincident(g30,g23)
    c: Coincident(g30,g23)
    c: Horizontal(g30)
    c: Coincident(g31,g20)
    c: Coincident(g31,g20)
    c: Horizontal(g31)
    c: Coincident(g32,g19)
    c: Coincident(g32,g19)
    c: Horizontal(g32)
    c: Coincident(g33,g18)
    c: Coincident(g33,g18)
    c: Horizontal(g33)
    c: Coincident(g34,g17)
    c: Coincident(g34,g17)
    c: Horizontal(g34)
    c: Coincident(g35,g16)
    c: Coincident(g35,g16)
    c: Coincident(g36,g15)
    c: Coincident(g36,g15)
    c: Coincident(g37,g11)
    c: Coincident(g37,g11)
    c: DistanceX(g10,g8) = 2.7
    c: PointOnObject(g10,g-5)
    c: Radius(g10) = 0.6
    c: Radius(g11) = 0.6
    c: Radius(g15) = 0.6
    c: Radius(g16) = 0.6
    c: Radius(g17) = 0.6
    c: Radius(g18) = 0.6
    c: Radius(g19) = 0.6
    c: Radius(g20) = 0.6
    c: Radius(g24) = 0.6
    c: Radius(g25) = 0.6
    c: Radius(g21) = 0.6
    c: Radius(g22) = 0.6
    c: Radius(g23) = 0.6
    c: Distance(g10,g11) = 3.825
    c: PointOnObject(g11,g-5)
    c: PointOnObject(g15,g36)
    c: PointOnObject(g16,g-5)
    c: PointOnObject(g17,g34)
    c: PointOnObject(g17,g-6)
    c: Distance(g12,g15) = 3.825
    c: Distance(g15,g16) = 3.825
    c: DistanceX(g16,g17) = 2.7
    c: DistanceX(g17,g18) = 2.7
    c: DistanceX(g18,g19) = 2.7
    c: DistanceX(g19,g20) = 2.7
    c: DistanceX(g20,g24) = 2.7
    c: DistanceX(g25,g21) = 2.7
    c: DistanceX(g21,g22) = 2.7
    c: DistanceX(g22,g23) = 2.7
    c: PointOnObject(g18,g33)
    c: PointOnObject(g18,g-6)
    c: PointOnObject(g19,g-6)
    c: PointOnObject(g19,g32)
    c: PointOnObject(g20,g31)
    c: PointOnObject(g20,g-6)
    c: PointOnObject(g24,g-6)
    c: DistanceX(g27,g27) = 2.5
    c: PointOnObject(g24,g27)
    c: DistanceX(g25,g25) = 0
    c: DistanceX(g24,g24) = 0
    c: PointOnObject(g21,g28)
    c: PointOnObject(g21,g-6)
    c: PointOnObject(g22,g29)
    c: PointOnObject(g22,g-6)
    c: PointOnObject(g23,g30)
    c: PointOnObject(g23,g-6)
FEATURE [PartDesign::Pad] Pad100
  BaseFeature = -> Pocket094
  Direction = (0,0,-1)
  Length = 3.95
  Length2 = 10
  Profile = -> Sketch190
  ReferenceAxis = -> Sketch190 [N_Axis]
  Refine = true
  Reversed = true
  Suppressed = false
  Type = 0
FEATURE [Sketcher::SketchObject] Sketch191
  ArcFitTolerance = 1e-06
  AttachmentSupport = -> [Pad100]
  ExternalGeometry = -> [Pad100]
  FullyConstrained = true
  MakeInternals = false
  MapMode = 5
  Placement = pos=(0,0,1.6) rot=(0,0,1;0rad)
  sketch-geometry (1):
    g0: Circle CenterX=8 CenterY=0 CenterZ=0 NormalX=0 NormalY=0 NormalZ=1 AngleXU=0 Radius=2.25
  constraints (2):
    c: Coincident(g0,g-3)
    c: Diameter(g0) = 4.5
FEATURE [PartDesign::Pad] Pad101
  BaseFeature = -> Pad100
  Direction = (0,0,1)
  Length = 4.9
  Length2 = 10
  Profile = -> Sketch191
  ReferenceAxis = -> Sketch191 [N_Axis]
  Refine = true
  Suppressed = false
  Type = 0
FEATURE [Sketcher::SketchObject] Sketch192
  ArcFitTolerance = 1e-06
  AttachmentSupport = -> [Pad101]
  ExternalGeometry = -> [Pad101]
  FullyConstrained = true
  MakeInternals = false
  MapMode = 5
  Placement = pos=(0,0,6.5) rot=(0,0,1;0rad)
  sketch-geometry (1):
    g0: Circle CenterX=8 CenterY=0 CenterZ=0 NormalX=0 NormalY=0 NormalZ=1 AngleXU=0 Radius=0.75
  constraints (2):
    c: Coincident(g0,g-3)
    c: Diameter(g0) = 1.5
FEATURE [PartDesign::Pocket] Pocket095
  BaseFeature = -> Pad101
  Direction = (0,0,-1)
  Length = 4.9
  Length2 = 5
  Profile = -> Sketch192
  ReferenceAxis = -> Sketch192 [N_Axis]
  Refine = true
  Suppressed = false
  Type = 0
FEATURE [Sketcher::SketchObject] Sketch193
  ArcFitTolerance = 1e-06
  AttachmentSupport = -> [Pocket095]
  ExternalGeometry = -> [Pocket095]
  FullyConstrained = true
  MakeInternals = false
  MapMode = 5
  Placement = pos=(0,0,1.6) rot=(0,0,1;0rad)
  sketch-geometry (1):
    g0: Circle CenterX=42.05 CenterY=0 CenterZ=0 NormalX=0 NormalY=0 NormalZ=1 AngleXU=0 Radius=2.475
  constraints (2):
    c: Coincident(g0,g-3)
    c: Diameter(g0) = 4.95
FEATURE [PartDesign::Pad] Pad102
  BaseFeature = -> Pocket095
  Direction = (0,0,1)
  Length = 6.5
  Length2 = 10
  Profile = -> Sketch193
  ReferenceAxis = -> Sketch193 [N_Axis]
  Refine = true
  Suppressed = false
  Type = 0
FEATURE [Sketcher::SketchObject] Sketch194
  ArcFitTolerance = 1e-06
  AttachmentSupport = -> [Pad102]
  ExternalGeometry = -> [Pad102]
  FullyConstrained = true
  MakeInternals = false
  MapMode = 5
  Placement = pos=(0,0,8.1) rot=(0,0,1;0rad)
  sketch-geometry (1):
    g0: Circle CenterX=42.05 CenterY=0 CenterZ=0 NormalX=0 NormalY=0 NormalZ=1 AngleXU=0 Radius=0.75
  constraints (2):
    c: Coincident(g0,g-3)
    c: Diameter(g0) = 1.5
FEATURE [PartDesign::Pocket] Pocket096
  BaseFeature = -> Pad102
  Direction = (0,0,-1)
  Length = 6.5
  Length2 = 5
  Profile = -> Sketch194
  ReferenceAxis = -> Sketch194 [N_Axis]
  Refine = true
  Suppressed = false
  Type = 0
FEATURE [PartDesign::Fillet] Fillet041
  Base = -> Pocket096 [Edge172,Edge85]
  BaseFeature = -> Pocket096
  Radius = 0.5
  Refine = true
  SupportTransform = false
  Suppressed = false
  UseAllEdges = false
FEATURE [Sketcher::SketchObject] Sketch195
  ArcFitTolerance = 1e-06
  AttachmentSupport = -> [Fillet041]
  ExternalGeometry = -> [Fillet041]
  FullyConstrained = true
  MakeInternals = false
  MapMode = 5
  Placement = pos=(0,0,0) rot=(1,0,0;3.14159rad)
  sketch-geometry (1):
    g0: Circle CenterX=38.9 CenterY=2.2 CenterZ=0 NormalX=0 NormalY=0 NormalZ=1 AngleXU=0 Radius=0.95
  constraints (3):
    c: DistanceX(g0,g-3) = 3.15
    c: Diameter(g0) = 1.9
    c: DistanceY(g0,g-3) = 3.35
FEATURE [PartDesign::Pad] Pad103
  BaseFeature = -> Fillet041
  Direction = (0,0,-1)
  Length = 2.2
  Length2 = 10
  Profile = -> Sketch195
  ReferenceAxis = -> Sketch195 [N_Axis]
  Refine = true
  Suppressed = false
  Type = 0
FEATURE [PartDesign::Fillet] Fillet042
  Base = -> Pad103 [Edge39]
  BaseFeature = -> Pad103
  Radius = 0.2
  Refine = true
  SupportTransform = false
  Suppressed = false
  UseAllEdges = false
FEATURE [Sketcher::SketchObject] Sketch355
  ArcFitTolerance = 1e-06
  AttachmentSupport = -> [Fillet042]
  ExternalGeometry = -> [Fillet042]
  FullyConstrained = true
  MakeInternals = false
  MapMode = 5
  Placement = pos=(0,0,1.6) rot=(0,0,1;0rad)
  sketch-geometry (4):
    g0: LineSegment StartX=-3.1 StartY=1.55 StartZ=0 EndX=-3.1 EndY=-1.55 EndZ=0
    g1: LineSegment StartX=-3.1 StartY=-1.55 StartZ=0 EndX=3.1 EndY=-1.55 EndZ=0
    g2: LineSegment StartX=3.1 StartY=-1.55 StartZ=0 EndX=3.1 EndY=1.55 EndZ=0
    g3: LineSegment StartX=3.1 StartY=1.55 StartZ=0 EndX=-3.1 EndY=1.55 EndZ=0
  constraints (12):
    c: Coincident(g0,g1)
    c: Coincident(g1,g2)
    c: Coincident(g2,g3)
    c: Coincident(g3,g0)
    c: Vertical(g0)
    c: Vertical(g2)
    c: Horizontal(g1)
    c: Horizontal(g3)
    c: DistanceX(g3,g3) = 6.2
    c: DistanceY(g0,g0) = 3.1
    c: DistanceX(g0,g-4) = 0.1
    c: DistanceY(g-4,g0) = 0.05
FEATURE [PartDesign::Pocket] Pocket171
  BaseFeature = -> Fillet042
  Direction = (0,0,-1)
  Length = 5
  Length2 = 5
  Profile = -> Sketch355
  ReferenceAxis = -> Sketch355 [N_Axis]
  Refine = true
  Suppressed = false
  Type = 0
FEATURE [PartDesign::Body] Body015  label="Right_Inner_Leg"
  AllowCompound = false
  Group = -> [Sketch187,Pad098,Sketch188,Pad099,Pocket093,Sketch189,Pocket094,Sketch190,Pad100,Sketch191,Pad101,Sketch192,Pocket095,Sketch193,Pad102,Sketch194,Pocket096,Fillet041,Sketch195,Pad103,Fillet042,Sketch355,Pocket171]
  Origin = -> Origin017
  Placement = pos=(27.8,-51,-6.5) rot=(-0.58,-0.58,0.58;2.0944rad)
  Tip = -> Pocket171
COMPONENT P7 — recipe-attached ("Waist", modeled in this document).
Construction recipe (the document's own serialized feature program — sketch geometry with constraints, then the solid features built on it; lengths are millimeters unless a unit is written):

FEATURE [Sketcher::SketchObject] Sketch203
  ArcFitTolerance = 1e-06
  AttachmentSupport = -> [XY_Plane019]
  FullyConstrained = true
  MakeInternals = false
  MapMode = 5
  sketch-geometry (4):
    g0: ArcOfCircle CenterX=0 CenterY=0 CenterZ=0 NormalX=0 NormalY=0 NormalZ=1 AngleXU=0 Radius=2.9 StartAngle=1.5708 EndAngle=4.71239
    g1: ArcOfCircle CenterX=6.5 CenterY=6.09966e-11 CenterZ=0 NormalX=0 NormalY=0 NormalZ=1 AngleXU=0 Radius=2.9 StartAngle=4.71239 EndAngle=7.85398
    g2: LineSegment StartX=-2.53925e-11 StartY=2.9 StartZ=0 EndX=6.5 EndY=2.9 EndZ=0
    g3: LineSegment StartX=4.6e-15 StartY=-2.9 StartZ=0 EndX=6.5 EndY=-2.9 EndZ=0
  constraints (9):
    c: Tangent(g0,g2) = 1.5708
    c: Tangent(g0,g3) = -1.5708
    c: Tangent(g1,g2) = 1.5708
    c: Tangent(g1,g3) = -1.5708
    c: Equal(g0,g1)
    c: Horizontal(g3)
    c: Coincident(g0,g-1)
    c: Diameter(g0) = 5.8
    c: DistanceX(g0,g1) = 6.5
FEATURE [PartDesign::Pad] Pad111
  Direction = (0,0,1)
  Length = 2.2
  Length2 = 10
  Profile = -> Sketch203
  ReferenceAxis = -> Sketch203 [N_Axis]
  Refine = true
  Suppressed = false
  Type = 0
FEATURE [Sketcher::SketchObject] Sketch204
  ArcFitTolerance = 1e-06
  AttachmentSupport = -> [Pad111]
  ExternalGeometry = -> [Pad111]
  FullyConstrained = true
  MakeInternals = false
  MapMode = 5
  Placement = pos=(0,0,2.2) rot=(0,0,1;0rad)
  sketch-geometry (1):
    g0: Circle CenterX=6.5 CenterY=0 CenterZ=0 NormalX=0 NormalY=0 NormalZ=1 AngleXU=0 Radius=2.9
  constraints (2):
    c: Coincident(g0,g-3)
    c: Equal(g0,g-3)
FEATURE [PartDesign::Pad] Pad112
  BaseFeature = -> Pad111
  Direction = (0,0,1)
  Length = 2
  Length2 = 10
  Profile = -> Sketch204
  ReferenceAxis = -> Sketch204 [N_Axis]
  Refine = true
  Suppressed = false
  Type = 0
FEATURE [Sketcher::SketchObject] Sketch205
  ArcFitTolerance = 1e-06
  AttachmentSupport = -> [Pad112]
  ExternalGeometry = -> [Pad112]
  FullyConstrained = true
  MakeInternals = false
  MapMode = 5
  Placement = pos=(0,0,4.2) rot=(0,0,1;0rad)
  sketch-geometry (1):
    g0: Circle CenterX=6.5 CenterY=0 CenterZ=0 NormalX=0 NormalY=0 NormalZ=1 AngleXU=0 Radius=1.5
  constraints (2):
    c: Coincident(g0,g-3)
    c: Diameter(g0) = 3
FEATURE [PartDesign::Pad] Pad113
  BaseFeature = -> Pad112
  Direction = (0,0,1)
  Length = 2
  Length2 = 10
  Profile = -> Sketch205
  ReferenceAxis = -> Sketch205 [N_Axis]
  Refine = true
  Suppressed = false
  Type = 0
FEATURE [Sketcher::SketchObject] Sketch206
  ArcFitTolerance = 1e-06
  AttachmentSupport = -> [Pad113]
  ExternalGeometry = -> [Pad113]
  FullyConstrained = true
  MakeInternals = false
  MapMode = 5
  Placement = pos=(0,0,6.2) rot=(0,0,1;0rad)
  sketch-geometry (4):
    g0: LineSegment StartX=9.55 StartY=1.5 StartZ=0 EndX=3.45 EndY=1.5 EndZ=0
    g1: LineSegment StartX=3.45 StartY=1.5 StartZ=0 EndX=3.45 EndY=-1.5 EndZ=0
    g2: LineSegment StartX=3.45 StartY=-1.5 StartZ=0 EndX=9.55 EndY=-1.5 EndZ=0
    g3: LineSegment StartX=9.55 StartY=-1.5 StartZ=0 EndX=9.55 EndY=1.5 EndZ=0
  constraints (12):
    c: Coincident(g0,g1)
    c: Coincident(g1,g2)
    c: Coincident(g2,g3)
    c: Coincident(g3,g0)
    c: Horizontal(g0)
    c: Horizontal(g2)
    c: Vertical(g1)
    c: Vertical(g3)
    c: DistanceY(g-3,g0) = 1.5
    c: DistanceY(g2,g-3) = 1.5
    c: DistanceX(g0,g-3) = 3.05
    c: DistanceX(g-3,g2) = 3.05
FEATURE [PartDesign::Pad] Pad114
  BaseFeature = -> Pad113
  Direction = (0,0,1)
  Length = 3.1
  Length2 = 10
  Profile = -> Sketch206
  ReferenceAxis = -> Sketch206 [N_Axis]
  Refine = true
  Suppressed = false
  Type = 0
FEATURE [Sketcher::SketchObject] Sketch207
  ArcFitTolerance = 1e-06
  AttachmentSupport = -> [Pad114]
  FullyConstrained = true
  MakeInternals = false
  MapMode = 5
  Placement = pos=(0,0,0) rot=(1,0,0;3.14159rad)
  sketch-geometry (1):
    g0: Circle CenterX=0 CenterY=0 CenterZ=0 NormalX=0 NormalY=0 NormalZ=1 AngleXU=0 Radius=1.5
  constraints (2):
    c: Coincident(g0,g-1)
    c: Diameter(g0) = 3
FEATURE [PartDesign::Pad] Pad115
  BaseFeature = -> Pad114
  Direction = (0,0,-1)
  Length = 4
  Length2 = 10
  Profile = -> Sketch207
  ReferenceAxis = -> Sketch207 [N_Axis]
  Refine = true
  Suppressed = false
  Type = 0
FEATURE [Sketcher::SketchObject] Sketch208
  ArcFitTolerance = 1e-06
  AttachmentSupport = -> [Pad115]
  ExternalGeometry = -> [Pad115]
  FullyConstrained = true
  MakeInternals = false
  MapMode = 5
  Placement = pos=(0,0,-4) rot=(1,0,0;3.14159rad)
  sketch-geometry (4):
    g0: ArcOfCircle CenterX=0 CenterY=0 CenterZ=0 NormalX=0 NormalY=0 NormalZ=1 AngleXU=0 Radius=1.5 StartAngle=0.841069 EndAngle=2.30052
    g1: ArcOfCircle CenterX=0 CenterY=0 CenterZ=0 NormalX=0 NormalY=0 NormalZ=1 AngleXU=0 Radius=1.5 StartAngle=3.98266 EndAngle=5.44212
    g2: LineSegment StartX=-1 StartY=1.11803 StartZ=0 EndX=-1 EndY=-1.11803 EndZ=0
    g3: LineSegment StartX=1 StartY=1.11803 StartZ=0 EndX=1 EndY=-1.11803 EndZ=0
  constraints (12):
    c: PointOnObject(g0,g-3)
    c: PointOnObject(g1,g-3)
    c: Coincident(g2,g0)
    c: Coincident(g2,g1)
    c: Coincident(g3,g0)
    c: Coincident(g3,g1)
    c: Vertical(g3)
    c: Vertical(g2)
    c: DistanceX(g0,g-1) = 1
    c: Coincident(g1,g-1)
    c: Coincident(g0,g1)
    c: DistanceX(g0,g0) = 1
FEATURE [PartDesign::Pad] Pad116
  BaseFeature = -> Pad115
  Direction = (0,0,-1)
  Length = 3.6
  Length2 = 10
  Profile = -> Sketch208
  ReferenceAxis = -> Sketch208 [N_Axis]
  Refine = true
  Suppressed = false
  Type = 0
FEATURE [Sketcher::SketchObject] Sketch209
  ArcFitTolerance = 1e-06
  AttachmentSupport = -> [Pad116]
  FullyConstrained = true
  MakeInternals = false
  MapMode = 5
  Placement = pos=(0,0,-7.6) rot=(1,0,0;3.14159rad)
  sketch-geometry (1):
    g0: Circle CenterX=0 CenterY=0 CenterZ=0 NormalX=0 NormalY=0 NormalZ=1 AngleXU=0 Radius=1.5
  constraints (2):
    c: Coincident(g0,g-1)
    c: Diameter(g0) = 3
FEATURE [PartDesign::Pad] Pad117
  BaseFeature = -> Pad116
  Direction = (0,0,-1)
  Length = 4
  Length2 = 10
  Profile = -> Sketch209
  ReferenceAxis = -> Sketch209 [N_Axis]
  Refine = true
  Suppressed = false
  Type = 0
FEATURE [Sketcher::SketchObject] Sketch210
  ArcFitTolerance = 1e-06
  AttachmentSupport = -> [Pad117]
  ExternalGeometry = -> [Pad117]
  FullyConstrained = true
  MakeInternals = false
  MapMode = 5
  Placement = pos=(0,0,-11.6) rot=(1,0,0;3.14159rad)
  sketch-geometry (4):
    g0: ArcOfCircle CenterX=0 CenterY=0 CenterZ=0 NormalX=0 NormalY=0 NormalZ=1 AngleXU=0 Radius=2.9 StartAngle=1.5708 EndAngle=4.71239
    g1: ArcOfCircle CenterX=6.5 CenterY=-6.09966e-11 CenterZ=0 NormalX=0 NormalY=0 NormalZ=1 AngleXU=0 Radius=2.9 StartAngle=4.71239 EndAngle=7.85398
    g2: LineSegment StartX=4.6e-15 StartY=2.9 StartZ=0 EndX=6.5 EndY=2.9 EndZ=0
    g3: LineSegment StartX=-5.44383e-11 StartY=-2.9 StartZ=0 EndX=6.5 EndY=-2.9 EndZ=0
  constraints (7):
    c: Tangent(g0,g2) = 1.5708
    c: Tangent(g0,g3) = -1.5708
    c: Tangent(g1,g2) = 1.5708
    c: Tangent(g1,g3) = -1.5708
    c: Coincident(g1,g-7)
    c: Coincident(g0,g-1)
    c: Coincident(g0,g-4)
FEATURE [PartDesign::Pad] Pad118
  BaseFeature = -> Pad117
  Direction = (0,0,-1)
  Length = 2.2
  Length2 = 10
  Profile = -> Sketch210
  ReferenceAxis = -> Sketch210 [N_Axis]
  Refine = true
  Suppressed = false
  Type = 0
FEATURE [Sketcher::SketchObject] Sketch211
  ArcFitTolerance = 1e-06
  AttachmentSupport = -> [Pad118]
  ExternalGeometry = -> [Pad118]
  FullyConstrained = true
  MakeInternals = false
  MapMode = 5
  Placement = pos=(0,0,-13.8) rot=(1,0,0;3.14159rad)
  sketch-geometry (1):
    g0: Circle CenterX=6.5 CenterY=0 CenterZ=0 NormalX=0 NormalY=0 NormalZ=1 AngleXU=0 Radius=2.9
  constraints (2):
    c: Coincident(g0,g-3)
    c: Equal(g0,g-3)
FEATURE [PartDesign::Pad] Pad119
  BaseFeature = -> Pad118
  Direction = (0,0,-1)
  Length = 2
  Length2 = 10
  Profile = -> Sketch211
  ReferenceAxis = -> Sketch211 [N_Axis]
  Refine = true
  Suppressed = false
  Type = 0
FEATURE [Sketcher::SketchObject] Sketch212
  ArcFitTolerance = 1e-06
  AttachmentSupport = -> [Pad119]
  ExternalGeometry = -> [Pad119]
  FullyConstrained = true
  MakeInternals = false
  MapMode = 5
  Placement = pos=(0,0,-15.8) rot=(1,0,0;3.14159rad)
  sketch-geometry (1):
    g0: Circle CenterX=6.5 CenterY=0 CenterZ=0 NormalX=0 NormalY=0 NormalZ=1 AngleXU=0 Radius=1.5
  constraints (2):
    c: Coincident(g0,g-3)
    c: Diameter(g0) = 3
FEATURE [PartDesign::Pad] Pad120
  BaseFeature = -> Pad119
  Direction = (0,0,-1)
  Length = 2
  Length2 = 10
  Profile = -> Sketch212
  ReferenceAxis = -> Sketch212 [N_Axis]
  Refine = true
  Suppressed = false
  Type = 0
FEATURE [Sketcher::SketchObject] Sketch213
  ArcFitTolerance = 1e-06
  AttachmentSupport = -> [Pad120]
  ExternalGeometry = -> [Pad120]
  FullyConstrained = true
  MakeInternals = false
  MapMode = 5
  Placement = pos=(0,0,-17.8) rot=(1,0,0;3.14159rad)
  sketch-geometry (4):
    g0: LineSegment StartX=3.45 StartY=1.5 StartZ=0 EndX=3.45 EndY=-1.5 EndZ=0
    g1: LineSegment StartX=3.45 StartY=-1.5 StartZ=0 EndX=9.55 EndY=-1.5 EndZ=0
    g2: LineSegment StartX=9.55 StartY=-1.5 StartZ=0 EndX=9.55 EndY=1.5 EndZ=0
    g3: LineSegment StartX=9.55 StartY=1.5 StartZ=0 EndX=3.45 EndY=1.5 EndZ=0
  constraints (12):
    c: Coincident(g0,g1)
    c: Coincident(g1,g2)
    c: Coincident(g2,g3)
    c: Coincident(g3,g0)
    c: Vertical(g0)
    c: Vertical(g2)
    c: Horizontal(g1)
    c: Horizontal(g3)
    c: DistanceX(g0,g-3) = 3.05
    c: DistanceX(g-3,g2) = 3.05
    c: DistanceY(g-3,g0) = 1.5
    c: DistanceY(g1,g-3) = 1.5
FEATURE [PartDesign::Pad] Pad121
  BaseFeature = -> Pad120
  Direction = (0,0,-1)
  Length = 3.1
  Length2 = 10
  Profile = -> Sketch213
  ReferenceAxis = -> Sketch213 [N_Axis]
  Refine = true
  Suppressed = false
  Type = 0
FEATURE [PartDesign::Pad] Pad205
  BaseFeature = -> Pad121
  Direction = (0,0,1)
  Length = 0.2
  Length2 = 10
  Profile = -> Pad121 [Face5]
  Refine = true
  Suppressed = false
  Type = 0
FEATURE [PartDesign::Pad] Pad206
  BaseFeature = -> Pad205
  Direction = (0,0,-1)
  Length = 0.2
  Length2 = 10
  Profile = -> Pad205 [Face8]
  Refine = true
  Suppressed = false
  Type = 0
FEATURE [PartDesign::Body] Body017  label="Waist"
  AllowCompound = false
  Group = -> [Sketch203,Pad111,Sketch204,Pad112,Sketch205,Pad113,Sketch206,Pad114,Sketch207,Pad115,Sketch208,Pad116,Sketch209,Pad117,Sketch210,Pad118,Sketch211,Pad119,Sketch212,Pad120,Sketch213,Pad121,Pad205,Pad206]
  Origin = -> Origin019
  Placement = pos=(44,-51,-1.42e-14) rot=(0,-1,0;4.71239rad)
  Tip = -> Pad206
COMPONENT P8 — recipe-attached ("Right_Inner_Leg001", modeled in this document).
Construction recipe (the document's own serialized feature program — sketch geometry with constraints, then the solid features built on it; lengths are millimeters unless a unit is written):

FEATURE [Sketcher::SketchObject] Sketch214
  ArcFitTolerance = 1e-06
  AttachmentSupport = -> [XY_Plane020]
  FullyConstrained = true
  MakeInternals = false
  MapMode = 5
  sketch-geometry (4):
    g0: LineSegment StartX=3e-16 StartY=5.55 StartZ=0 EndX=42.05 EndY=5.55 EndZ=0
    g1: ArcOfCircle CenterX=42.05 CenterY=3.35631e-11 CenterZ=0 NormalX=0 NormalY=0 NormalZ=1 AngleXU=0 Radius=5.55 StartAngle=4.71239 EndAngle=7.85398
    g2: LineSegment StartX=42.05 StartY=-5.55 StartZ=0 EndX=0 EndY=-5.55 EndZ=0
    g3: ArcOfCircle CenterX=0 CenterY=0 CenterZ=0 NormalX=0 NormalY=0 NormalZ=1 AngleXU=0 Radius=5.55 StartAngle=1.5708 EndAngle=4.71239
  constraints (13):
    c: PointOnObject(g0,g-2)
    c: Horizontal(g0)
    c: Coincident(g1,g0)
    c: Coincident(g2,g1)
    c: PointOnObject(g2,g-2)
    c: Horizontal(g2)
    c: Coincident(g3,g2)
    c: Coincident(g3,g0)
    c: DistanceX(g0,g0) = 42.05
    c: Radius(g3) = 5.55
    c: Radius(g1) = 5.55
    c: Coincident(g3,g-1)
    c: PointOnObject(g1,g-1)
FEATURE [PartDesign::Pad] Pad122
  Direction = (0,0,1)
  Length = 1.6
  Length2 = 10
  Profile = -> Sketch214
  ReferenceAxis = -> Sketch214 [N_Axis]
  Refine = true
  Suppressed = false
  Type = 0
FEATURE [Sketcher::SketchObject] Sketch215
  ArcFitTolerance = 1e-06
  AttachmentSupport = -> [Pad122]
  ExternalGeometry = -> [Pad122]
  FullyConstrained = true
  MakeInternals = false
  MapMode = 5
  Placement = pos=(0,0,0) rot=(1,0,0;3.14159rad)
  sketch-geometry (8):
    g0: LineSegment StartX=19.17 StartY=5.55 StartZ=0 EndX=0 EndY=5.55 EndZ=0
    g1: ArcOfCircle CenterX=0 CenterY=1e-16 CenterZ=0 NormalX=0 NormalY=0 NormalZ=1 AngleXU=0 Radius=5.55 StartAngle=1.5708 EndAngle=4.71239
    g2: LineSegment StartX=-1e-15 StartY=-5.55 StartZ=0 EndX=35.05 EndY=-5.55 EndZ=0
    g3: LineSegment StartX=19.17 StartY=5.55 StartZ=0 EndX=19.17 EndY=7.05 EndZ=0
    g4: LineSegment StartX=19.17 StartY=7.05 StartZ=0 EndX=7.1e-15 EndY=7.05 EndZ=0
    g5: ArcOfCircle CenterX=0 CenterY=1e-16 CenterZ=0 NormalX=0 NormalY=0 NormalZ=1 AngleXU=0 Radius=7.05 StartAngle=1.5708 EndAngle=4.71239
    g6: LineSegment StartX=5e-15 StartY=-7.05 StartZ=0 EndX=35.05 EndY=-7.05 EndZ=0
    g7: LineSegment StartX=35.05 StartY=-5.55 StartZ=0 EndX=35.05 EndY=-7.05 EndZ=0
  constraints (24):
    c: Coincident(g0,g-4)
    c: Coincident(g1,g0)
    c: Coincident(g1,g-5)
    c: Coincident(g2,g1)
    c: PointOnObject(g2,g-5)
    c: PointOnObject(g0,g-3)
    c: DistanceX(g2,g2) = 35.05
    c: DistanceX(g0,g0) = 19.17
    c: Coincident(g1,g-1)
    c: Coincident(g3,g0)
    c: Vertical(g3)
    c: Coincident(g4,g3)
    c: PointOnObject(g4,g-2)
    c: Horizontal(g4)
    c: Coincident(g5,g4)
    c: PointOnObject(g5,g-2)
    c: Coincident(g6,g5)
    c: Horizontal(g6)
    c: Coincident(g7,g2)
    c: Coincident(g7,g6)
    c: Vertical(g7)
    c: DistanceY(g3,g3) = 1.5
    c: DistanceY(g7,g7) = 1.5
    c: Coincident(g5,g1)
FEATURE [PartDesign::Pad] Pad123
  BaseFeature = -> Pad122
  Direction = (0,0,-1)
  Length = 4.05
  Length2 = 10
  Profile = -> Sketch215
  ReferenceAxis = -> Sketch215 [N_Axis]
  Refine = true
  Reversed = true
  Suppressed = false
  Type = 0
FEATURE [PartDesign::Pocket] Pocket098
  BaseFeature = -> Pad123
  Direction = (0,0,1)
  Length = 0.1
  Length2 = 5
  Profile = -> Sketch215
  ReferenceAxis = -> Sketch215 [N_Axis]
  Refine = true
  Suppressed = false
  Type = 0
FEATURE [Sketcher::SketchObject] Sketch216
  ArcFitTolerance = 1e-06
  AttachmentSupport = -> [Pocket098]
  FullyConstrained = true
  MakeInternals = false
  MapMode = 5
  Placement = pos=(0,0,0) rot=(1,0,0;3.14159rad)
  sketch-geometry (5):
    g0: LineSegment StartX=-3 StartY=1.5 StartZ=0 EndX=-3 EndY=-1.5 EndZ=0
    g1: LineSegment StartX=-3 StartY=-1.5 StartZ=0 EndX=3 EndY=-1.5 EndZ=0
    g2: LineSegment StartX=3 StartY=-1.5 StartZ=0 EndX=3 EndY=1.5 EndZ=0
    g3: LineSegment StartX=3 StartY=1.5 StartZ=0 EndX=-3 EndY=1.5 EndZ=0
    g4: Circle CenterX=8 CenterY=0 CenterZ=0 NormalX=0 NormalY=0 NormalZ=1 AngleXU=0 Radius=0.75
  constraints (15):
    c: Coincident(g0,g1)
    c: Coincident(g1,g2)
    c: Coincident(g2,g3)
    c: Coincident(g3,g0)
    c: Vertical(g0)
    c: Vertical(g2)
    c: Horizontal(g1)
    c: Horizontal(g3)
    c: DistanceY(g-1,g0) = 1.5
    c: DistanceY(g0,g-1) = 1.5
    c: DistanceX(g0,g-1) = 3
    c: DistanceX(g-1,g2) = 3
    c: PointOnObject(g4,g-1)
    c: Diameter(g4) = 1.5
    c: DistanceX(g-1,g4) = 8
FEATURE [PartDesign::Pocket] Pocket099
  BaseFeature = -> Pocket098
  Direction = (0,0,1)
  Length = 1.6
  Length2 = 5
  Profile = -> Sketch216
  ReferenceAxis = -> Sketch216 [N_Axis]
  Refine = true
  Suppressed = false
  Type = 0
FEATURE [Sketcher::SketchObject] Sketch217
  ArcFitTolerance = 1e-06
  AttachmentSupport = -> [Pocket099]
  ExternalGeometry = -> [Pocket099]
  FullyConstrained = true
  MakeInternals = false
  MapMode = 5
  Placement = pos=(0,0,0.1) rot=(1,0,0;3.14159rad)
  sketch-geometry (38):
    g0: ArcOfCircle CenterX=18.57 CenterY=7.05 CenterZ=0 NormalX=0 NormalY=0 NormalZ=1 AngleXU=0 Radius=0.6 StartAngle=-4.4e-15 EndAngle=3.14159
    g1: ArcOfCircle CenterX=14.67 CenterY=7.05 CenterZ=0 NormalX=0 NormalY=0 NormalZ=1 AngleXU=0 Radius=0.6 StartAngle=-8e-15 EndAngle=3.14159
    g2: ArcOfCircle CenterX=10.77 CenterY=7.05 CenterZ=0 NormalX=0 NormalY=0 NormalZ=1 AngleXU=0 Radius=0.6 StartAngle=6e-16 EndAngle=3.14159
    g3: ArcOfCircle CenterX=6.87 CenterY=7.05 CenterZ=0 NormalX=0 NormalY=0 NormalZ=1 AngleXU=0 Radius=0.6 StartAngle=-4.4e-15 EndAngle=3.14159
    g4: LineSegment StartX=19.17 StartY=7.05 StartZ=0 EndX=17.97 EndY=7.05 EndZ=0
    g5: LineSegment StartX=15.27 StartY=7.05 StartZ=0 EndX=14.07 EndY=7.05 EndZ=0
    g6: LineSegment StartX=11.37 StartY=7.05 StartZ=0 EndX=10.17 EndY=7.05 EndZ=0
    g7: LineSegment StartX=7.47 StartY=7.05 StartZ=0 EndX=6.27 EndY=7.05 EndZ=0
    g8: ArcOfCircle CenterX=2.97 CenterY=7.05 CenterZ=0 NormalX=0 NormalY=0 NormalZ=1 AngleXU=0 Radius=0.6 StartAngle=-1.8e-15 EndAngle=3.14159
    g9: LineSegment StartX=3.57 StartY=7.05 StartZ=0 EndX=2.37 EndY=7.05 EndZ=0
    g10: ArcOfCircle CenterX=-0.927604 CenterY=6.98871 CenterZ=0 NormalX=0 NormalY=0 NormalZ=1 AngleXU=0 Radius=0.6 StartAngle=0.0893917 EndAngle=3.31612
    g11: ArcOfCircle CenterX=-5.30424 CenterY=4.64408 CenterZ=0 NormalX=0 NormalY=0 NormalZ=1 AngleXU=0 Radius=0.6 StartAngle=0.809094 EndAngle=4.03582
    g12: ArcOfCircle CenterX=-7.05 CenterY=0 CenterZ=0 NormalX=0 NormalY=0 NormalZ=1 AngleXU=0 Radius=0.6 StartAngle=1.52823 EndAngle=4.75496
    g13: LineSegment StartX=-7.02447 StartY=0.599457 StartZ=0 EndX=-7.02447 EndY=-0.599457 EndZ=0
    g14: LineSegment StartX=-0.33 StartY=7.04227 StartZ=0 EndX=-1.51849 EndY=6.88453 EndZ=0
    g15: ArcOfCircle CenterX=-5.28202 CenterY=-4.63063 CenterZ=0 NormalX=0 NormalY=0 NormalZ=1 AngleXU=0 Radius=0.6 StartAngle=2.29058 EndAngle=5.43217
    g16: ArcOfCircle CenterX=-0.922566 CenterY=-6.98938 CenterZ=0 NormalX=0 NormalY=0 NormalZ=1 AngleXU=0 Radius=0.6 StartAngle=2.96779 EndAngle=6.19451
    g17: ArcOfCircle CenterX=2.97508 CenterY=-7.05 CenterZ=0 NormalX=0 NormalY=0 NormalZ=1 AngleXU=0 Radius=0.6 StartAngle=3.14159 EndAngle=6.28319
    g18: ArcOfCircle CenterX=6.87508 CenterY=-7.05 CenterZ=0 NormalX=0 NormalY=0 NormalZ=1 AngleXU=0 Radius=0.6 StartAngle=3.14159 EndAngle=6.28319
    g19: ArcOfCircle CenterX=10.7751 CenterY=-7.05 CenterZ=0 NormalX=0 NormalY=0 NormalZ=1 AngleXU=0 Radius=0.6 StartAngle=3.14159 EndAngle=6.28319
    g20: ArcOfCircle CenterX=14.6751 CenterY=-7.05 CenterZ=0 NormalX=0 NormalY=0 NormalZ=1 AngleXU=0 Radius=0.6 StartAngle=3.14159 EndAngle=6.28319
    g21: ArcOfCircle CenterX=23.7751 CenterY=-7.05 CenterZ=0 NormalX=0 NormalY=0 NormalZ=1 AngleXU=0 Radius=0.6 StartAngle=3.14159 EndAngle=6.28319
    g22: ArcOfCircle CenterX=27.6751 CenterY=-7.05 CenterZ=0 NormalX=0 NormalY=0 NormalZ=1 AngleXU=0 Radius=0.6 StartAngle=3.14159 EndAngle=6.28319
    g23: ArcOfCircle CenterX=31.5751 CenterY=-7.05 CenterZ=0 NormalX=0 NormalY=0 NormalZ=1 AngleXU=0 Radius=0.6 StartAngle=3.14159 EndAngle=6.28319
    g24: ArcOfCircle CenterX=18.5751 CenterY=-7.05 CenterZ=0 NormalX=0 NormalY=0 NormalZ=1 AngleXU=0 Radius=0.6 StartAngle=3.14159 EndAngle=4.71239
    g25: ArcOfCircle CenterX=19.8751 CenterY=-7.05 CenterZ=0 NormalX=0 NormalY=0 NormalZ=1 AngleXU=0 Radius=0.6 StartAngle=4.71239 EndAngle=6.28319
    g26: LineSegment StartX=19.8751 StartY=-7.65 StartZ=0 EndX=18.5751 EndY=-7.65 EndZ=0
    g27: LineSegment StartX=20.4751 StartY=-7.05 StartZ=0 EndX=17.9751 EndY=-7.05 EndZ=0
    g28: LineSegment StartX=24.3751 StartY=-7.05 StartZ=0 EndX=23.1751 EndY=-7.05 EndZ=0
    g29: LineSegment StartX=28.2751 StartY=-7.05 StartZ=0 EndX=27.0751 EndY=-7.05 EndZ=0
    g30: LineSegment StartX=32.1751 StartY=-7.05 StartZ=0 EndX=30.9751 EndY=-7.05 EndZ=0
    g31: LineSegment StartX=15.2751 StartY=-7.05 StartZ=0 EndX=14.0751 EndY=-7.05 EndZ=0
    g32: LineSegment StartX=11.3751 StartY=-7.05 StartZ=0 EndX=10.1751 EndY=-7.05 EndZ=0
    g33: LineSegment StartX=7.47508 StartY=-7.05 StartZ=0 EndX=6.27508 EndY=-7.05 EndZ=0
    g34: LineSegment StartX=3.57508 StartY=-7.05 StartZ=0 EndX=2.37508 EndY=-7.05 EndZ=0
    g35: LineSegment StartX=-0.324923 StartY=-7.04251 StartZ=0 EndX=-1.51353 EndY=-6.88562 EndZ=0
    g36: LineSegment StartX=-4.88649 StartY=-5.0818 StartZ=0 EndX=-5.67755 EndY=-4.17946 EndZ=0
    g37: LineSegment StartX=-4.89015 StartY=5.07828 StartZ=0 EndX=-5.67992 EndY=4.17625 EndZ=0
  constraints (132):
    c: Coincident(g4,g0)
    c: Coincident(g4,g0)
    c: Horizontal(g4)
    c: Coincident(g5,g1)
    c: Coincident(g5,g1)
    c: Horizontal(g5)
    c: Coincident(g6,g2)
    c: Coincident(g6,g2)
    c: Horizontal(g6)
    c: Coincident(g7,g3)
    c: Coincident(g7,g3)
    c: Horizontal(g7)
    c: Coincident(g9,g8)
    c: Coincident(g9,g8)
    c: Horizontal(g9)
    c: Radius(g0) = 0.6
    c: Radius(g1) = 0.6
    c: Radius(g2) = 0.6
    c: Radius(g3) = 0.6
    c: DistanceX(g3,g2) = 2.7
    c: Coincident(g0,g-3)
    c: PointOnObject(g0,g4)
    c: PointOnObject(g1,g-4)
    c: PointOnObject(g1,g5)
    c: DistanceX(g1,g0) = 2.7
    c: DistanceX(g2,g1) = 2.7
    c: DistanceX(g8,g3) = 2.7
    c: PointOnObject(g2,g6)
    c: PointOnObject(g2,g-4)
    c: PointOnObject(g3,g-4)
    c: PointOnObject(g3,g7)
    c: PointOnObject(g8,g-4)
    c: PointOnObject(g8,g9)
    c: Radius(g8) = 0.6
    c: PointOnObject(g10,g-5)
    c: PointOnObject(g10,g-5)
    c: PointOnObject(g11,g-5)
    c: PointOnObject(g11,g-5)
    c: PointOnObject(g12,g-5)
    c: PointOnObject(g12,g-5)
    c: PointOnObject(g12,g-1)
    c: PointOnObject(g12,g-5)
    c: Radius(g12) = 0.6
    c: Coincident(g13,g12)
    c: Coincident(g13,g12)
    c: Coincident(g14,g10)
    c: Coincident(g14,g10)
    c: PointOnObject(g15,g-5)
    c: PointOnObject(g15,g-5)
    c: PointOnObject(g16,g-5)
    c: PointOnObject(g16,g-5)
    c: Coincident(g26,g25)
    c: Coincident(g26,g24)
    c: Horizontal(g26)
    c: Coincident(g27,g25)
    c: Coincident(g27,g24)
    c: Horizontal(g27)
    c: Coincident(g28,g21)
    c: Coincident(g28,g21)
    c: Horizontal(g28)
    c: Coincident(g29,g22)
    c: Coincident(g29,g22)
    c: Horizontal(g29)
    c: Coincident(g30,g23)
    c: Coincident(g30,g23)
    c: Horizontal(g30)
    c: Coincident(g31,g20)
    c: Coincident(g31,g20)
    c: Horizontal(g31)
    c: Coincident(g32,g19)
    c: Coincident(g32,g19)
    c: Horizontal(g32)
    c: Coincident(g33,g18)
    c: Coincident(g33,g18)
    c: Horizontal(g33)
    c: Coincident(g34,g17)
    c: Coincident(g34,g17)
    c: Horizontal(g34)
    c: Coincident(g35,g16)
    c: Coincident(g35,g16)
    c: Coincident(g36,g15)
    c: Coincident(g36,g15)
    c: Coincident(g37,g11)
    c: Coincident(g37,g11)
    c: DistanceX(g10,g8) = 2.7
    c: PointOnObject(g10,g-5)
    c: Radius(g10) = 0.6
    c: Radius(g11) = 0.6
    c: Radius(g15) = 0.6
    c: Radius(g16) = 0.6
    c: Radius(g17) = 0.6
    c: Radius(g18) = 0.6
    c: Radius(g19) = 0.6
    c: Radius(g20) = 0.6
    c: Radius(g24) = 0.6
    c: Radius(g25) = 0.6
    c: Radius(g21) = 0.6
    c: Radius(g22) = 0.6
    c: Radius(g23) = 0.6
    c: Distance(g10,g11) = 3.825
    c: PointOnObject(g11,g-5)
    c: PointOnObject(g15,g36)
    c: PointOnObject(g16,g-5)
    c: PointOnObject(g17,g34)
    c: PointOnObject(g17,g-6)
    c: Distance(g12,g15) = 3.825
    c: Distance(g15,g16) = 3.825
    c: DistanceX(g16,g17) = 2.7
    c: DistanceX(g17,g18) = 2.7
    c: DistanceX(g18,g19) = 2.7
    c: DistanceX(g19,g20) = 2.7
    c: DistanceX(g20,g24) = 2.7
    c: DistanceX(g25,g21) = 2.7
    c: DistanceX(g21,g22) = 2.7
    c: DistanceX(g22,g23) = 2.7
    c: PointOnObject(g18,g33)
    c: PointOnObject(g18,g-6)
    c: PointOnObject(g19,g-6)
    c: PointOnObject(g19,g32)
    c: PointOnObject(g20,g31)
    c: PointOnObject(g20,g-6)
    c: PointOnObject(g24,g-6)
    c: DistanceX(g27,g27) = 2.5
    c: PointOnObject(g24,g27)
    c: DistanceX(g25,g25) = 0
    c: DistanceX(g24,g24) = 0
    c: PointOnObject(g21,g28)
    c: PointOnObject(g21,g-6)
    c: PointOnObject(g22,g29)
    c: PointOnObject(g22,g-6)
    c: PointOnObject(g23,g30)
    c: PointOnObject(g23,g-6)
FEATURE [PartDesign::Pad] Pad124
  BaseFeature = -> Pocket099
  Direction = (0,0,-1)
  Length = 3.95
  Length2 = 10
  Profile = -> Sketch217
  ReferenceAxis = -> Sketch217 [N_Axis]
  Refine = true
  Reversed = true
  Suppressed = false
  Type = 0
FEATURE [Sketcher::SketchObject] Sketch218
  ArcFitTolerance = 1e-06
  AttachmentSupport = -> [Pad124]
  ExternalGeometry = -> [Pad124]
  FullyConstrained = true
  MakeInternals = false
  MapMode = 5
  Placement = pos=(0,0,1.6) rot=(0,0,1;0rad)
  sketch-geometry (1):
    g0: Circle CenterX=8 CenterY=0 CenterZ=0 NormalX=0 NormalY=0 NormalZ=1 AngleXU=0 Radius=2.25
  constraints (2):
    c: Coincident(g0,g-3)
    c: Diameter(g0) = 4.5
FEATURE [PartDesign::Pad] Pad125
  BaseFeature = -> Pad124
  Direction = (0,0,1)
  Length = 4.9
  Length2 = 10
  Profile = -> Sketch218
  ReferenceAxis = -> Sketch218 [N_Axis]
  Refine = true
  Suppressed = false
  Type = 0
FEATURE [Sketcher::SketchObject] Sketch219
  ArcFitTolerance = 1e-06
  AttachmentSupport = -> [Pad125]
  ExternalGeometry = -> [Pad125]
  FullyConstrained = true
  MakeInternals = false
  MapMode = 5
  Placement = pos=(0,0,6.5) rot=(0,0,1;0rad)
  sketch-geometry (1):
    g0: Circle CenterX=8 CenterY=0 CenterZ=0 NormalX=0 NormalY=0 NormalZ=1 AngleXU=0 Radius=0.75
  constraints (2):
    c: Coincident(g0,g-3)
    c: Diameter(g0) = 1.5
FEATURE [PartDesign::Pocket] Pocket100
  BaseFeature = -> Pad125
  Direction = (0,0,-1)
  Length = 4.9
  Length2 = 5
  Profile = -> Sketch219
  ReferenceAxis = -> Sketch219 [N_Axis]
  Refine = true
  Suppressed = false
  Type = 0
FEATURE [Sketcher::SketchObject] Sketch220
  ArcFitTolerance = 1e-06
  AttachmentSupport = -> [Pocket100]
  ExternalGeometry = -> [Pocket100]
  FullyConstrained = true
  MakeInternals = false
  MapMode = 5
  Placement = pos=(0,0,1.6) rot=(0,0,1;0rad)
  sketch-geometry (1):
    g0: Circle CenterX=42.05 CenterY=0 CenterZ=0 NormalX=0 NormalY=0 NormalZ=1 AngleXU=0 Radius=2.475
  constraints (2):
    c: Coincident(g0,g-3)
    c: Diameter(g0) = 4.95
FEATURE [PartDesign::Pad] Pad126
  BaseFeature = -> Pocket100
  Direction = (0,0,1)
  Length = 6.5
  Length2 = 10
  Profile = -> Sketch220
  ReferenceAxis = -> Sketch220 [N_Axis]
  Refine = true
  Suppressed = false
  Type = 0
FEATURE [Sketcher::SketchObject] Sketch221
  ArcFitTolerance = 1e-06
  AttachmentSupport = -> [Pad126]
  ExternalGeometry = -> [Pad126]
  FullyConstrained = true
  MakeInternals = false
  MapMode = 5
  Placement = pos=(0,0,8.1) rot=(0,0,1;0rad)
  sketch-geometry (1):
    g0: Circle CenterX=42.05 CenterY=0 CenterZ=0 NormalX=0 NormalY=0 NormalZ=1 AngleXU=0 Radius=0.75
  constraints (2):
    c: Coincident(g0,g-3)
    c: Diameter(g0) = 1.5
FEATURE [PartDesign::Pocket] Pocket101
  BaseFeature = -> Pad126
  Direction = (0,0,-1)
  Length = 6.5
  Length2 = 5
  Profile = -> Sketch221
  ReferenceAxis = -> Sketch221 [N_Axis]
  Refine = true
  Suppressed = false
  Type = 0
FEATURE [PartDesign::Fillet] Fillet044
  Base = -> Pocket101 [Edge172,Edge85]
  BaseFeature = -> Pocket101
  Radius = 0.5
  Refine = true
  SupportTransform = false
  Suppressed = false
  UseAllEdges = false
FEATURE [Sketcher::SketchObject] Sketch222
  ArcFitTolerance = 1e-06
  AttachmentSupport = -> [Fillet044]
  ExternalGeometry = -> [Fillet044]
  FullyConstrained = true
  MakeInternals = false
  MapMode = 5
  Placement = pos=(0,0,0) rot=(1,0,0;3.14159rad)
  sketch-geometry (1):
    g0: Circle CenterX=38.9 CenterY=2.2 CenterZ=0 NormalX=0 NormalY=0 NormalZ=1 AngleXU=0 Radius=0.95
  constraints (3):
    c: DistanceX(g0,g-3) = 3.15
    c: Diameter(g0) = 1.9
    c: DistanceY(g0,g-3) = 3.35
FEATURE [PartDesign::Pad] Pad127
  BaseFeature = -> Fillet044
  Direction = (0,0,-1)
  Length = 2.2
  Length2 = 10
  Profile = -> Sketch222
  ReferenceAxis = -> Sketch222 [N_Axis]
  Refine = true
  Suppressed = false
  Type = 0
FEATURE [PartDesign::Fillet] Fillet045
  Base = -> Pad127 [Edge39]
  BaseFeature = -> Pad127
  Radius = 0.2
  Refine = true
  SupportTransform = false
  Suppressed = false
  UseAllEdges = false
FEATURE [Sketcher::SketchObject] Sketch356
  ArcFitTolerance = 1e-06
  AttachmentSupport = -> [Fillet045]
  ExternalGeometry = -> [Fillet045]
  FullyConstrained = true
  MakeInternals = false
  MapMode = 5
  Placement = pos=(0,0,1.6) rot=(0,0,1;0rad)
  sketch-geometry (4):
    g0: LineSegment StartX=-3.1 StartY=1.55 StartZ=0 EndX=-3.1 EndY=-1.55 EndZ=0
    g1: LineSegment StartX=-3.1 StartY=-1.55 StartZ=0 EndX=3.1 EndY=-1.55 EndZ=0
    g2: LineSegment StartX=3.1 StartY=-1.55 StartZ=0 EndX=3.1 EndY=1.55 EndZ=0
    g3: LineSegment StartX=3.1 StartY=1.55 StartZ=0 EndX=-3.1 EndY=1.55 EndZ=0
  constraints (12):
    c: Coincident(g0,g1)
    c: Coincident(g1,g2)
    c: Coincident(g2,g3)
    c: Coincident(g3,g0)
    c: Vertical(g0)
    c: Vertical(g2)
    c: Horizontal(g1)
    c: Horizontal(g3)
    c: DistanceX(g3,g3) = 6.2
    c: DistanceY(g2,g2) = 3.1
    c: DistanceX(g0,g-4) = 0.1
    c: DistanceY(g-4,g0) = 0.05
FEATURE [PartDesign::Pocket] Pocket172
  BaseFeature = -> Fillet045
  Direction = (0,0,-1)
  Length = 5
  Length2 = 5
  Profile = -> Sketch356
  ReferenceAxis = -> Sketch356 [N_Axis]
  Refine = true
  Suppressed = false
  Type = 0
FEATURE [PartDesign::Body] Body018  label="Right_Inner_Leg001"
  AllowCompound = false
  Group = -> [Sketch214,Pad122,Sketch215,Pad123,Pocket098,Sketch216,Pocket099,Sketch217,Pad124,Sketch218,Pad125,Sketch219,Pocket100,Sketch220,Pad126,Sketch221,Pocket101,Fillet044,Sketch222,Pad127,Fillet045,Sketch356,Pocket172]
  Origin = -> Origin020
  Placement = pos=(-10.89,-44.5046,-8.89) rot=(0.577486,0.577079,-0.577486;4.18838rad)
  Tip = -> Pocket172
COMPONENT P9 — recipe-attached ("Scoop_Connector", modeled in this document).
Construction recipe (the document's own serialized feature program — sketch geometry with constraints, then the solid features built on it; lengths are millimeters unless a unit is written):

FEATURE [Sketcher::SketchObject] Sketch243
  ArcFitTolerance = 1e-06
  AttachmentSupport = -> [XY_Plane022]
  FullyConstrained = true
  MakeInternals = false
  MapMode = 5
  sketch-geometry (4):
    g0: ArcOfCircle CenterX=0 CenterY=0 CenterZ=0 NormalX=0 NormalY=0 NormalZ=1 AngleXU=0 Radius=3 StartAngle=1.5708 EndAngle=4.71239
    g1: ArcOfCircle CenterX=19.75 CenterY=0 CenterZ=0 NormalX=0 NormalY=0 NormalZ=1 AngleXU=0 Radius=3 StartAngle=4.71239 EndAngle=7.85398
    g2: LineSegment StartX=-5e-16 StartY=3 StartZ=0 EndX=19.75 EndY=3 EndZ=0
    g3: LineSegment StartX=-6e-16 StartY=-3 StartZ=0 EndX=19.75 EndY=-3 EndZ=0
  constraints (9):
    c: Tangent(g0,g2) = 1.5708
    c: Tangent(g0,g3) = -1.5708
    c: Tangent(g1,g2) = 1.5708
    c: Tangent(g1,g3) = -1.5708
    c: Equal(g0,g1)
    c: Horizontal(g3)
    c: Coincident(g0,g-1)
    c: Diameter(g0) = 6
    c: DistanceX(g0,g1) = 19.75
FEATURE [PartDesign::Pad] Pad139
  Direction = (0,0,1)
  Length = 2
  Length2 = 10
  Profile = -> Sketch243
  ReferenceAxis = -> Sketch243 [N_Axis]
  Refine = true
  Suppressed = false
  Type = 0
FEATURE [Sketcher::SketchObject] Sketch244
  ArcFitTolerance = 1e-06
  AttachmentSupport = -> [Pad139]
  ExternalGeometry = -> [Pad139]
  FullyConstrained = true
  MakeInternals = false
  MapMode = 5
  Placement = pos=(0,0,2) rot=(0,0,1;0rad)
  sketch-geometry (2):
    g0: Circle CenterX=0 CenterY=0 CenterZ=0 NormalX=0 NormalY=0 NormalZ=1 AngleXU=0 Radius=1.5
    g1: Circle CenterX=19.75 CenterY=0 CenterZ=0 NormalX=0 NormalY=0 NormalZ=1 AngleXU=0 Radius=1.5
  constraints (4):
    c: Coincident(g0,g-1)
    c: Coincident(g1,g-4)
    c: Diameter(g0) = 3
    c: Diameter(g1) = 3
FEATURE [PartDesign::Pad] Pad140
  BaseFeature = -> Pad139
  Direction = (0,0,1)
  Length = 16
  Length2 = 10
  Profile = -> Sketch244
  ReferenceAxis = -> Sketch244 [N_Axis]
  Refine = true
  Suppressed = false
  Type = 0
FEATURE [Sketcher::SketchObject] Sketch245
  ArcFitTolerance = 1e-06
  AttachmentSupport = -> [Pad140]
  ExternalGeometry = -> [Pad140]
  FullyConstrained = true
  MakeInternals = false
  MapMode = 5
  Placement = pos=(0,0,18) rot=(0,0,1;0rad)
  sketch-geometry (4):
    g0: ArcOfCircle CenterX=0 CenterY=0 CenterZ=0 NormalX=0 NormalY=0 NormalZ=1 AngleXU=0 Radius=3 StartAngle=1.5708 EndAngle=4.71239
    g1: ArcOfCircle CenterX=19.75 CenterY=0 CenterZ=0 NormalX=0 NormalY=0 NormalZ=1 AngleXU=0 Radius=3 StartAngle=4.71239 EndAngle=7.85398
    g2: LineSegment StartX=-5e-16 StartY=3 StartZ=0 EndX=19.75 EndY=3 EndZ=0
    g3: LineSegment StartX=0 StartY=-3 StartZ=0 EndX=19.75 EndY=-3 EndZ=0
  constraints (8):
    c: Tangent(g0,g2) = 1.5708
    c: Tangent(g0,g3) = -1.5708
    c: Tangent(g1,g2) = 1.5708
    c: Tangent(g1,g3) = -1.5708
    c: Equal(g0,g1)
    c: Diameter(g0) = 6
    c: Coincident(g-1,g0)
    c: Coincident(g1,g-3)
FEATURE [PartDesign::Pad] Pad141
  BaseFeature = -> Pad140
  Direction = (0,0,1)
  Length = 2
  Length2 = 10
  Profile = -> Sketch245
  ReferenceAxis = -> Sketch245 [N_Axis]
  Refine = true
  Suppressed = false
  Type = 0
FEATURE [Sketcher::SketchObject] Sketch246
  ArcFitTolerance = 1e-06
  AttachmentSupport = -> [Pad141]
  FullyConstrained = true
  MakeInternals = false
  MapMode = 5
  Placement = pos=(0,0,20) rot=(0,0,1;0rad)
  sketch-geometry (1):
    g0: Circle CenterX=0 CenterY=0 CenterZ=0 NormalX=0 NormalY=0 NormalZ=1 AngleXU=0 Radius=1.5
  constraints (2):
    c: Coincident(g0,g-1)
    c: Diameter(g0) = 3
FEATURE [PartDesign::Pad] Pad142
  BaseFeature = -> Pad141
  Direction = (0,0,1)
  Length = 0.5
  Length2 = 10
  Profile = -> Sketch246
  ReferenceAxis = -> Sketch246 [N_Axis]
  Refine = true
  Suppressed = false
  Type = 0
FEATURE [Sketcher::SketchObject] Sketch247
  ArcFitTolerance = 1e-06
  AttachmentSupport = -> [Pad142]
  FullyConstrained = true
  MakeInternals = false
  MapMode = 5
  Placement = pos=(0,0,0) rot=(1,0,0;3.14159rad)
  sketch-geometry (1):
    g0: Circle CenterX=0 CenterY=0 CenterZ=0 NormalX=0 NormalY=0 NormalZ=1 AngleXU=0 Radius=1.5
  constraints (2):
    c: Coincident(g0,g-1)
    c: Diameter(g0) = 3
FEATURE [PartDesign::Pad] Pad143
  BaseFeature = -> Pad142
  Direction = (0,0,-1)
  Length = 0.5
  Length2 = 10
  Profile = -> Sketch247
  ReferenceAxis = -> Sketch247 [N_Axis]
  Refine = true
  Suppressed = false
  Type = 0
FEATURE [PartDesign::Pad] Pad212
  BaseFeature = -> Pad143
  Direction = (0,0,1)
  Length = 0.1
  Length2 = 10
  Profile = -> Pad143 [Face5]
  Refine = true
  Suppressed = false
  Type = 0
FEATURE [PartDesign::Pad] Pad213
  BaseFeature = -> Pad212
  Direction = (0,0,-1)
  Length = 0.1
  Length2 = 10
  Profile = -> Pad212 [Face4]
  Refine = true
  Suppressed = false
  Type = 0
FEATURE [Sketcher::SketchObject] Sketch353
  ArcFitTolerance = 1e-06
  AttachmentSupport = -> [Pad213]
  ExternalGeometry = -> [Pad213]
  FullyConstrained = true
  MakeInternals = false
  MapMode = 5
  Placement = pos=(0,0,20.5) rot=(0,0,1;0rad)
  sketch-geometry (1):
    g0: Circle CenterX=0 CenterY=0 CenterZ=0 NormalX=0 NormalY=0 NormalZ=1 AngleXU=0 Radius=1.6
  constraints (2):
    c: Coincident(g0,g-1)
    c: Radius(g0) = 1.6
FEATURE [PartDesign::Pocket] Pocket170
  BaseFeature = -> Pad213
  Direction = (0,0,-1)
  Length = 22
  Length2 = 5
  Profile = -> Sketch353
  ReferenceAxis = -> Sketch353 [N_Axis]
  Refine = true
  Suppressed = false
  Type = 0
FEATURE [PartDesign::Body] Body020  label="Scoop_Connector"
  AllowCompound = false
  Group = -> [Sketch243,Pad139,Sketch244,Pad140,Sketch245,Pad141,Sketch246,Pad142,Sketch247,Pad143,Pad212,Pad213,Sketch353,Pocket170]
  Origin = -> Origin022
  Placement = pos=(28.2,-60.15,0) rot=(0.58,0.58,0.58;2.0944rad)
  Tip = -> Pocket170
COMPONENT P10 — recipe-attached ("Scoop", modeled in this document).
Construction recipe (the document's own serialized feature program — sketch geometry with constraints, then the solid features built on it; lengths are millimeters unless a unit is written):

FEATURE [Sketcher::SketchObject] Sketch248
  ArcFitTolerance = 1e-06
  AttachmentSupport = -> [XY_Plane023]
  FullyConstrained = true
  MakeInternals = false
  MapMode = 5
  sketch-geometry (6):
    g0: LineSegment StartX=0 StartY=0 StartZ=0 EndX=0 EndY=1.4 EndZ=0
    g1: LineSegment StartX=0 StartY=1.4 StartZ=0 EndX=13.5 EndY=1.4 EndZ=0
    g2: LineSegment StartX=13.5 StartY=1.4 StartZ=0 EndX=13.5 EndY=21.4 EndZ=0
    g3: LineSegment StartX=13.5 StartY=21.4 StartZ=0 EndX=15.2 EndY=21.4 EndZ=0
    g4: LineSegment StartX=15.2 StartY=21.4 StartZ=0 EndX=15.2 EndY=0 EndZ=0
    g5: LineSegment StartX=15.2 StartY=0 StartZ=0 EndX=0 EndY=0 EndZ=0
  constraints (17):
    c: Coincident(g0,g-1)
    c: PointOnObject(g0,g-2)
    c: Coincident(g1,g0)
    c: Horizontal(g1)
    c: Coincident(g2,g1)
    c: Vertical(g2)
    c: Coincident(g3,g2)
    c: Horizontal(g3)
    c: Coincident(g4,g3)
    c: PointOnObject(g4,g-1)
    c: Vertical(g4)
    c: Coincident(g5,g4)
    c: Coincident(g5,g0)
    c: DistanceY(g0,g0) = 1.4
    c: DistanceX(g3,g3) = 1.7
    c: DistanceX(g1,g1) = 13.5
    c: DistanceY(g2,g2) = 20
FEATURE [PartDesign::Pad] Pad144
  Direction = (0,0,1)
  Length = 36.3
  Length2 = 10
  Profile = -> Sketch248
  ReferenceAxis = -> Sketch248 [N_Axis]
  Refine = true
  Suppressed = false
  Type = 0
FEATURE [Sketcher::SketchObject] Sketch249
  ArcFitTolerance = 1e-06
  AttachmentSupport = -> [Pad144]
  ExternalGeometry = -> [Pad144]
  FullyConstrained = true
  MakeInternals = false
  MapMode = 5
  Placement = pos=(0,0,36.3) rot=(0,0,1;0rad)
  sketch-geometry (4):
    g0: LineSegment StartX=15.2 StartY=15.6 StartZ=0 EndX=20.0363 EndY=14.3311 EndZ=0
    g1: LineSegment StartX=15.2 StartY=7.3 StartZ=0 EndX=20.0363 EndY=8.56892 EndZ=0
    g2: ArcOfCircle CenterX=19.2 CenterY=11.45 CenterZ=0 NormalX=0 NormalY=0 NormalZ=1 AngleXU=0 Radius=3 StartAngle=4.9949 EndAngle=7.57147
    g3: LineSegment StartX=15.2 StartY=7.3 StartZ=0 EndX=15.2 EndY=15.6 EndZ=0
  constraints (13):
    c: PointOnObject(g0,g-3)
    c: Coincident(g2,g0)
    c: Coincident(g2,g1)
    c: DistanceY(g1,g0) = 8.3
    c: Diameter(g2) = 6
    c: DistanceX(g0,g2) = 4
    c: DistanceX(g1,g0) = 0
    c: DistanceY(g0,g-3) = 5.8
    c: Distance(g0,g0) = 5
    c: Distance(g1,g1) = 5
    c: PointOnObject(g1,g-3)
    c: Coincident(g3,g1)
    c: Coincident(g3,g0)
FEATURE [PartDesign::Pad] Pad145
  BaseFeature = -> Pad144
  Direction = (0,0,1)
  Length = 36.3
  Length2 = 10
  Profile = -> Sketch249
  ReferenceAxis = -> Sketch249 [N_Axis]
  Refine = true
  Reversed = true
  Suppressed = false
  Type = 0
FEATURE [PartDesign::Pocket] Pocket111
  BaseFeature = -> Pad145
  Direction = (0,0,-1)
  Length = 28.2
  Length2 = 5
  Profile = -> Sketch249
  ReferenceAxis = -> Sketch249 [N_Axis]
  Refine = true
  Suppressed = false
  Type = 0
FEATURE [PartDesign::Pad] Pad146
  BaseFeature = -> Pocket111
  Direction = (0,0,1)
  Length = 8.1
  Length2 = 10
  Profile = -> Sketch249
  ReferenceAxis = -> Sketch249 [N_Axis]
  Refine = true
  Reversed = true
  Suppressed = false
  Type = 0
FEATURE [PartDesign::Pocket] Pocket112
  BaseFeature = -> Pad146
  Direction = (0,0,-1)
  Length = 5.1
  Length2 = 5
  Profile = -> Sketch249
  ReferenceAxis = -> Sketch249 [N_Axis]
  Refine = true
  Suppressed = false
  Type = 0
FEATURE [Sketcher::SketchObject] Sketch250
  ArcFitTolerance = 1e-06
  AttachmentSupport = -> [Pocket112]
  ExternalGeometry = -> [Pocket112]
  FullyConstrained = true
  MakeInternals = false
  MapMode = 5
  Placement = pos=(0,0,0) rot=(1,0,0;3.14159rad)
  sketch-geometry (4):
    g0: LineSegment StartX=20.0363 StartY=-8.56892 StartZ=0 EndX=15.2 EndY=-7.3 EndZ=0
    g1: LineSegment StartX=15.2 StartY=-7.3 StartZ=0 EndX=15.2 EndY=-15.6 EndZ=0
    g2: LineSegment StartX=15.2 StartY=-15.6 StartZ=0 EndX=20.0363 EndY=-14.3311 EndZ=0
    g3: ArcOfCircle CenterX=19.2 CenterY=-11.45 CenterZ=0 NormalX=0 NormalY=0 NormalZ=1 AngleXU=0 Radius=3 StartAngle=4.9949 EndAngle=7.57147
  constraints (9):
    c: Coincident(g0,g-4)
    c: Coincident(g0,g-3)
    c: Coincident(g1,g0)
    c: Coincident(g1,g-5)
    c: Coincident(g2,g1)
    c: Coincident(g2,g-5)
    c: Coincident(g3,g0)
    c: Coincident(g3,g2)
    c: Coincident(g3,g-4)
FEATURE [PartDesign::Pocket] Pocket113
  BaseFeature = -> Pocket112
  Direction = (0,0,1)
  Length = 5.1
  Length2 = 5
  Profile = -> Sketch250
  ReferenceAxis = -> Sketch250 [N_Axis]
  Refine = true
  Suppressed = false
  Type = 0
FEATURE [Sketcher::SketchObject] Sketch251
  ArcFitTolerance = 1e-06
  AttachmentSupport = -> [Pocket113]
  ExternalGeometry = -> [Pocket113]
  FullyConstrained = true
  MakeInternals = false
  MapMode = 5
  Placement = pos=(0,0,8.1) rot=(0,0,1;0rad)
  sketch-geometry (4):
    g0: ArcOfCircle CenterX=19.2 CenterY=11.45 CenterZ=0 NormalX=0 NormalY=0 NormalZ=1 AngleXU=0 Radius=1.55 StartAngle=4.71239 EndAngle=7.85398
    g1: LineSegment StartX=19.2 StartY=9.9 StartZ=0 EndX=15.2 EndY=9.9 EndZ=0
    g2: LineSegment StartX=19.2 StartY=13 StartZ=0 EndX=15.2 EndY=13 EndZ=0
    g3: LineSegment StartX=15.2 StartY=9.9 StartZ=0 EndX=15.2 EndY=13 EndZ=0
  constraints (12):
    c: Coincident(g0,g-3)
    c: Diameter(g0) = 3.1
    c: Horizontal(g1)
    c: Coincident(g2,g0)
    c: Horizontal(g2)
    c: Coincident(g1,g0)
    c: DistanceX(g0,g0) = 0
    c: DistanceX(g0,g0) = 0
    c: PointOnObject(g2,g-4)
    c: PointOnObject(g1,g-4)
    c: Coincident(g3,g1)
    c: Coincident(g3,g2)
FEATURE [PartDesign::Pocket] Pocket114
  BaseFeature = -> Pocket113
  Direction = (0,0,-1)
  Length = 2
  Length2 = 5
  Profile = -> Sketch251
  ReferenceAxis = -> Sketch251 [N_Axis]
  Refine = true
  Suppressed = false
  Type = 0
FEATURE [PartDesign::Pocket] Pocket115
  BaseFeature = -> Pocket114
  Direction = (0,0,-1)
  Length = 22
  Length2 = 5
  Profile = -> Sketch251
  ReferenceAxis = -> Sketch251 [N_Axis]
  Refine = true
  Reversed = true
  Suppressed = false
  Type = 0
FEATURE [Sketcher::SketchObject] Sketch252
  ArcFitTolerance = 1e-06
  AttachmentSupport = -> [Pocket115]
  ExternalGeometry = -> [Pocket115]
  FullyConstrained = true
  MakeInternals = false
  MapMode = 5
  Placement = pos=(15.2,0,0) rot=(0.57735,0.57735,0.57735;2.0944rad)
  sketch-geometry (8):
    g0: LineSegment StartX=9.9 StartY=30.1 StartZ=0 EndX=9.9 EndY=28.2 EndZ=0
    g1: LineSegment StartX=9.9 StartY=28.2 StartZ=0 EndX=13 EndY=28.2 EndZ=0
    g2: LineSegment StartX=13 StartY=28.2 StartZ=0 EndX=13 EndY=30.1 EndZ=0
    g3: LineSegment StartX=13 StartY=30.1 StartZ=0 EndX=9.9 EndY=30.1 EndZ=0
    g4: LineSegment StartX=9.9 StartY=6.1 StartZ=0 EndX=13 EndY=6.1 EndZ=0
    g5: LineSegment StartX=13 StartY=6.1 StartZ=0 EndX=13 EndY=8.1 EndZ=0
    g6: LineSegment StartX=13 StartY=8.1 StartZ=0 EndX=9.9 EndY=8.1 EndZ=0
    g7: LineSegment StartX=9.9 StartY=8.1 StartZ=0 EndX=9.9 EndY=6.1 EndZ=0
  constraints (20):
    c: Coincident(g0,g1)
    c: Coincident(g1,g2)
    c: Coincident(g2,g3)
    c: Coincident(g3,g0)
    c: Vertical(g0)
    c: Vertical(g2)
    c: Horizontal(g1)
    c: Horizontal(g3)
    c: Coincident(g0,g-4)
    c: Coincident(g1,g-3)
    c: Coincident(g4,g5)
    c: Coincident(g5,g6)
    c: Coincident(g6,g7)
    c: Coincident(g7,g4)
    c: Horizontal(g4)
    c: Horizontal(g6)
    c: Vertical(g5)
    c: Vertical(g7)
    c: Coincident(g4,g-6)
    c: Coincident(g5,g-5)
FEATURE [PartDesign::Pocket] Pocket116
  BaseFeature = -> Pocket115
  Direction = (-1,0,0)
  Length = 1.7
  Length2 = 5
  Profile = -> Sketch252
  ReferenceAxis = -> Sketch252 [N_Axis]
  Refine = true
  Suppressed = false
  Type = 0
FEATURE [Sketcher::SketchObject] Sketch253
  ArcFitTolerance = 1e-06
  AttachmentSupport = -> [Pocket116]
  ExternalGeometry = -> [Pocket116]
  FullyConstrained = true
  MakeInternals = false
  MapMode = 5
  Placement = pos=(0,0,36.3) rot=(0,0,1;0rad)
  sketch-geometry (4):
    g0: LineSegment StartX=13.5 StartY=21.4 StartZ=0 EndX=13.5 EndY=1.4 EndZ=0
    g1: LineSegment StartX=13.5 StartY=1.4 StartZ=0 EndX=2 EndY=1.4 EndZ=0
    g2: ArcOfCircle CenterX=2 CenterY=2.2 CenterZ=0 NormalX=0 NormalY=0 NormalZ=1 AngleXU=0 Radius=0.8 StartAngle=4.71239 EndAngle=5.71572
    g3: LineSegment StartX=2.67461 StartY=1.77 StartZ=0 EndX=13.5 EndY=21.4 EndZ=0
  constraints (11):
    c: Coincident(g0,g-3)
    c: Coincident(g0,g-4)
    c: Coincident(g1,g0)
    c: PointOnObject(g1,g-4)
    c: DistanceX(g-4,g1) = 2
    c: Coincident(g2,g1)
    c: Coincident(g3,g2)
    c: Coincident(g3,g0)
    c: DistanceX(g2,g1) = 0
    c: Radius(g2) = 0.8
    c: DistanceY(g2,g2) = 0.43
FEATURE [PartDesign::Pad] Pad147
  BaseFeature = -> Pocket116
  Direction = (0,0,1)
  Length = 36.3
  Length2 = 10
  Profile = -> Sketch253
  ReferenceAxis = -> Sketch253 [N_Axis]
  Refine = true
  Reversed = true
  Suppressed = false
  Type = 0
FEATURE [PartDesign::Pocket] Pocket117
  BaseFeature = -> Pad147
  Direction = (0,0,-1)
  Length = 34
  Length2 = 5
  Profile = -> Sketch253
  ReferenceAxis = -> Sketch253 [N_Axis]
  Refine = true
  Suppressed = false
  Type = 0
FEATURE [PartDesign::Pad] Pad148
  BaseFeature = -> Pocket117
  Direction = (0,0,1)
  Length = 2.3
  Length2 = 10
  Profile = -> Sketch253
  ReferenceAxis = -> Sketch253 [N_Axis]
  Refine = true
  Reversed = true
  Suppressed = false
  Type = 0
FEATURE [PartDesign::Fillet] Fillet047
  Base = -> Pad148 [Edge7,Edge20,Edge5,Edge18,Edge6]
  BaseFeature = -> Pad148
  Radius = 0.5
  Refine = true
  SupportTransform = false
  Suppressed = false
  UseAllEdges = false
FEATURE [PartDesign::Body] Body021  label="Scoop"
  AllowCompound = false
  Group = -> [Sketch248,Pad144,Sketch249,Pad145,Pocket111,Pad146,Pocket112,Sketch250,Pocket113,Sketch251,Pocket114,Pocket115,Sketch252,Pocket116,Sketch253,Pad147,Pocket117,Pad148,Fillet047]
  Origin = -> Origin023
  Placement = pos=(20.05,-79.35,-11.45) rot=(0.58,0.58,0.58;2.0944rad)
  Tip = -> Fillet047
COMPONENT P11 — recipe-attached ("Rear_Torso", modeled in this document).
Construction recipe (the document's own serialized feature program — sketch geometry with constraints, then the solid features built on it; lengths are millimeters unless a unit is written):

FEATURE [Sketcher::SketchObject] Sketch254
  ArcFitTolerance = 1e-06
  AttachmentSupport = -> [XY_Plane024]
  FullyConstrained = false
  MakeInternals = false
  MapMode = 5
  sketch-geometry (37):
    g0: LineSegment StartX=-6.44 StartY=-43 StartZ=0 EndX=-6.44 EndY=-41.5 EndZ=0
    g1: LineSegment StartX=-6.44 StartY=-41.5 StartZ=0 EndX=-7.54 EndY=-41.5 EndZ=0
    g2: ArcOfCircle CenterX=-7.54 CenterY=-40.5 CenterZ=0 NormalX=0 NormalY=0 NormalZ=1 AngleXU=0 Radius=1 StartAngle=3.14159 EndAngle=4.71239
    g3: ArcOfCircle CenterX=-5.94 CenterY=-41 CenterZ=0 NormalX=0 NormalY=0 NormalZ=1 AngleXU=0 Radius=1 StartAngle=3e-16 EndAngle=1.5708
    g4: LineSegment StartX=-6.44 StartY=-43 StartZ=0 EndX=-6.44 EndY=-47 EndZ=0
    g5: ArcOfCircle CenterX=-5.44 CenterY=-47 CenterZ=0 NormalX=0 NormalY=0 NormalZ=1 AngleXU=0 Radius=1 StartAngle=3.14159 EndAngle=4.71239
    g6: ArcOfCircle CenterX=3.86 CenterY=-47 CenterZ=0 NormalX=0 NormalY=0 NormalZ=1 AngleXU=0 Radius=1 StartAngle=4.71239 EndAngle=6.28319
    g7: ArcOfCircle CenterX=5.96 CenterY=-40.5 CenterZ=0 NormalX=0 NormalY=0 NormalZ=1 AngleXU=0 Radius=1 StartAngle=4.71239 EndAngle=6.28319
    g8: ArcOfCircle CenterX=4.36 CenterY=-41 CenterZ=0 NormalX=0 NormalY=0 NormalZ=1 AngleXU=0 Radius=1 StartAngle=1.5708 EndAngle=3.14159
    g9: ArcOfCircle CenterX=6.46 CenterY=-26 CenterZ=0 NormalX=0 NormalY=0 NormalZ=1 AngleXU=0 Radius=1 StartAngle=1.5708 EndAngle=3.14159
    g10: ArcOfCircle CenterX=8.21 CenterY=-25.5 CenterZ=0 NormalX=0 NormalY=0 NormalZ=1 AngleXU=0 Radius=1 StartAngle=4.71239 EndAngle=6.28319
    g11: ArcOfCircle CenterX=8.21 CenterY=0.5 CenterZ=0 NormalX=0 NormalY=0 NormalZ=1 AngleXU=0 Radius=1 StartAngle=6.39466e-10 EndAngle=1.5708
    g12: ArcOfCircle CenterX=-9.79 CenterY=0.5 CenterZ=0 NormalX=0 NormalY=0 NormalZ=1 AngleXU=0 Radius=1 StartAngle=1.5708 EndAngle=3.14159
    g13: ArcOfCircle CenterX=-9.79 CenterY=-25.5 CenterZ=0 NormalX=0 NormalY=0 NormalZ=1 AngleXU=0 Radius=1 StartAngle=3.14159 EndAngle=4.71239
    g14: ArcOfCircle CenterX=-8.04 CenterY=-26 CenterZ=0 NormalX=0 NormalY=0 NormalZ=1 AngleXU=0 Radius=1 StartAngle=-9e-16 EndAngle=1.5708
    g15: LineSegment StartX=-4.94 StartY=-41 StartZ=0 EndX=-4.94 EndY=-41.5 EndZ=0
    g16: LineSegment StartX=-4.94 StartY=-41.5 StartZ=0 EndX=3.36 EndY=-41.5 EndZ=0
    g17: LineSegment StartX=3.36 StartY=-41.5 StartZ=0 EndX=3.36 EndY=-41 EndZ=0
    g18: LineSegment StartX=5.96 StartY=-41.5 StartZ=0 EndX=4.86 EndY=-41.5 EndZ=0
    g19: LineSegment StartX=4.86 StartY=-41.5 StartZ=0 EndX=4.86 EndY=-47 EndZ=0
    g20: LineSegment StartX=3.86 StartY=-48 StartZ=0 EndX=-5.44 EndY=-48 EndZ=0
    g21: LineSegment StartX=4.36 StartY=-40 StartZ=0 EndX=5.46 EndY=-40 EndZ=0
    g22: LineSegment StartX=6.96 StartY=-40.5 StartZ=0 EndX=6.96 EndY=-26.5 EndZ=0
    g23: LineSegment StartX=8.21 StartY=-26.5 StartZ=0 EndX=6.96 EndY=-26.5 EndZ=0
    g24: LineSegment StartX=5.46 StartY=-26 StartZ=0 EndX=5.46 EndY=-40 EndZ=0
    g25: LineSegment StartX=6.46 StartY=-25 StartZ=0 EndX=7.71 EndY=-25 EndZ=0
    g26: LineSegment StartX=7.71 StartY=-25 StartZ=0 EndX=7.71 EndY=2.80835e-10 EndZ=0
    g27: LineSegment StartX=9.21 StartY=0.5 StartZ=0 EndX=9.21 EndY=-25.5 EndZ=0
    g28: LineSegment StartX=8.21 StartY=1.5 StartZ=0 EndX=-9.79 EndY=1.5 EndZ=0
    g29: LineSegment StartX=7.71 StartY=2.80835e-10 StartZ=0 EndX=-9.29 EndY=2.80835e-10 EndZ=0
    g30: LineSegment StartX=-9.29 StartY=2.80835e-10 StartZ=0 EndX=-9.29 EndY=-25 EndZ=0
    g31: LineSegment StartX=-8.04 StartY=-25 StartZ=0 EndX=-9.29 EndY=-25 EndZ=0
    g32: LineSegment StartX=-10.79 StartY=0.5 StartZ=0 EndX=-10.79 EndY=-25.5 EndZ=0
    g33: LineSegment StartX=-9.79 StartY=-26.5 StartZ=0 EndX=-8.54 EndY=-26.5 EndZ=0
    g34: LineSegment StartX=-7.04 StartY=-26 StartZ=0 EndX=-7.04 EndY=-40 EndZ=0
    g35: LineSegment StartX=-5.94 StartY=-40 StartZ=0 EndX=-7.04 EndY=-40 EndZ=0
    g36: LineSegment StartX=-8.54 StartY=-40.5 StartZ=0 EndX=-8.54 EndY=-26.5 EndZ=0
  constraints (74):
    c: Coincident(g0,g-10)
    c: Coincident(g0,g-11)
    c: Coincident(g1,g0)
    c: Coincident(g1,g-12)
    c: Coincident(g2,g1)
    c: Coincident(g2,g-13)
    c: Tangent(g2,g-12)
    c: Coincident(g3,g-7)
    c: Tangent(g3,g-6) = -1.5708
    c: Coincident(g4,g0)
    c: Coincident(g4,g-53)
    c: Coincident(g5,g4)
    c: Tangent(g5,g-52) = -1.5708
    c: Coincident(g6,g-50)
    c: Tangent(g6,g-49) = -1.5708
    c: Tangent(g7,g-19) = -1.5708
    c: Coincident(g7,g-23)
    c: Tangent(g8,g-21) = -1.5708
    c: Coincident(g8,g-21)
    c: Coincident(g9,g-30)
    c: Tangent(g9,g-29) = -1.5708
    c: Tangent(g10,g-28) = -1.5708
    c: Coincident(g10,g-32)
    c: Tangent(g11,g-33) = -1.5708
    c: Coincident(g11,g-33)
    c: Tangent(g12,g-37) = -1.5708
    c: Coincident(g12,g-38)
    c: Tangent(g13,g-42) = -1.5708
    c: Coincident(g13,g-43)
    c: Tangent(g14,g-40) = -1.5708
    c: Coincident(g14,g-41)
    c: Coincident(g15,g3)
    c: Coincident(g15,g-8)
    c: Coincident(g16,g15)
    c: Coincident(g16,g-15)
    c: Coincident(g17,g16)
    c: Coincident(g17,g8)
    c: Coincident(g18,g7)
    c: Coincident(g18,g-18)
    c: Coincident(g19,g18)
    c: Coincident(g19,g6)
    c: Coincident(g20,g6)
    c: Coincident(g20,g5)
    c: Coincident(g21,g8)
    c: Coincident(g21,g-22)
    c: Coincident(g22,g7)
    c: Coincident(g22,g-27)
    c: Coincident(g23,g10)
    c: Coincident(g23,g22)
    c: Coincident(g24,g9)
    c: Coincident(g24,g21)
    c: Coincident(g25,g9)
    c: Coincident(g25,g-31)
    c: Coincident(g26,g25)
    c: Coincident(g26,g-31)
    c: Coincident(g27,g10)
    c: Coincident(g27,g11)
    c: Coincident(g28,g11)
    c: Coincident(g28,g12)
    c: Coincident(g29,g26)
    c: Coincident(g29,g-36)
    c: Coincident(g30,g29)
    c: Coincident(g30,g-36)
    c: Coincident(g31,g14)
    c: Coincident(g31,g30)
    c: Tangent(g32,g13) = -1.5708
    c: Coincident(g33,g13)
    c: Coincident(g33,g-44)
    c: Coincident(g34,g14)
    c: Coincident(g34,g-14)
    c: Coincident(g35,g3)
    c: Coincident(g35,g34)
    c: Coincident(g36,g2)
    c: Coincident(g36,g33)
FEATURE [PartDesign::Pad] Pad149
  Direction = (0,0,1)
  Length = 3
  Length2 = 10
  Profile = -> Sketch254
  ReferenceAxis = -> Sketch254 [N_Axis]
  Refine = true
  Reversed = true
  Suppressed = false
  Type = 0
FEATURE [Sketcher::SketchObject] Sketch255
  ArcFitTolerance = 1e-06
  AttachmentSupport = -> [Pad149]
  ExternalGeometry = -> [Pad149]
  FullyConstrained = true
  MakeInternals = false
  MapMode = 5
  Placement = pos=(0,0,-3) rot=(1,0,0;3.14159rad)
  sketch-geometry (16):
    g0: LineSegment StartX=-4.94 StartY=41.5 StartZ=0 EndX=3.36 EndY=41.5 EndZ=0
    g1: LineSegment StartX=-4.94 StartY=41.5 StartZ=0 EndX=-4.94 EndY=41 EndZ=0
    g2: ArcOfCircle CenterX=-5.94 CenterY=41 CenterZ=0 NormalX=0 NormalY=0 NormalZ=1 AngleXU=0 Radius=1 StartAngle=4.71239 EndAngle=6.28319
    g3: LineSegment StartX=-5.94 StartY=40 StartZ=0 EndX=-7.04 EndY=40 EndZ=0
    g4: LineSegment StartX=-7.04 StartY=40 StartZ=0 EndX=-7.04 EndY=26 EndZ=0
    g5: ArcOfCircle CenterX=-8.04 CenterY=26 CenterZ=0 NormalX=0 NormalY=0 NormalZ=1 AngleXU=0 Radius=1 StartAngle=4.71239 EndAngle=6.28319
    g6: LineSegment StartX=-8.04 StartY=25 StartZ=0 EndX=-9.29 EndY=25 EndZ=0
    g7: LineSegment StartX=-9.29 StartY=25 StartZ=0 EndX=-9.29 EndY=-2.80835e-10 EndZ=0
    g8: LineSegment StartX=-9.29 StartY=-2.80835e-10 StartZ=0 EndX=7.71 EndY=-2.80835e-10 EndZ=0
    g9: LineSegment StartX=7.71 StartY=-2.80835e-10 StartZ=0 EndX=7.71 EndY=25 EndZ=0
    g10: LineSegment StartX=7.71 StartY=25 StartZ=0 EndX=6.46 EndY=25 EndZ=0
    g11: ArcOfCircle CenterX=6.46 CenterY=26 CenterZ=0 NormalX=0 NormalY=0 NormalZ=1 AngleXU=0 Radius=1 StartAngle=3.14159 EndAngle=4.71239
    g12: LineSegment StartX=5.46 StartY=26 StartZ=0 EndX=5.46 EndY=40 EndZ=0
    g13: ArcOfCircle CenterX=4.36 CenterY=41 CenterZ=0 NormalX=0 NormalY=0 NormalZ=1 AngleXU=0 Radius=1 StartAngle=3.14159 EndAngle=4.71239
    g14: LineSegment StartX=3.36 StartY=41 StartZ=0 EndX=3.36 EndY=41.5 EndZ=0
    g15: LineSegment StartX=5.46 StartY=40 StartZ=0 EndX=4.36 EndY=40 EndZ=0
  constraints (32):
    c: Coincident(g0,g-15)
    c: Coincident(g1,g0)
    c: Coincident(g1,g-15)
    c: Coincident(g2,g1)
    c: Tangent(g2,g-14) = -1.5708
    c: Coincident(g3,g2)
    c: Coincident(g3,g-13)
    c: Coincident(g4,g3)
    c: Coincident(g4,g-12)
    c: Coincident(g5,g4)
    c: Tangent(g5,g-11) = -1.5708
    c: Coincident(g6,g5)
    c: Coincident(g6,g-10)
    c: Coincident(g7,g6)
    c: Coincident(g7,g-9)
    c: Coincident(g8,g7)
    c: Coincident(g8,g-8)
    c: Coincident(g9,g8)
    c: Coincident(g9,g-7)
    c: Coincident(g10,g9)
    c: Coincident(g10,g-6)
    c: Coincident(g11,g10)
    c: Tangent(g11,g-5) = -1.5708
    c: Coincident(g12,g-4)
    c: Coincident(g12,g11)
    c: Coincident(g0,g-3)
    c: Tangent(g13,g-16) = -1.5708
    c: Coincident(g13,g-16)
    c: Coincident(g15,g12)
    c: Coincident(g15,g13)
    c: Coincident(g14,g0)
    c: Coincident(g14,g13)
FEATURE [PartDesign::Pad] Pad150
  BaseFeature = -> Pad149
  Direction = (0,0,-1)
  Length = 1.5
  Length2 = 10
  Profile = -> Sketch255
  ReferenceAxis = -> Sketch255 [N_Axis]
  Refine = true
  Reversed = true
  Suppressed = false
  Type = 0
FEATURE [Sketcher::SketchObject] Sketch257
  ArcFitTolerance = 1e-06
  AttachmentSupport = -> [Pad150]
  ExternalGeometry = -> [Pad150]
  FullyConstrained = false
  MakeInternals = false
  MapMode = 5
  Placement = pos=(-8.54,4.4e-15,0) rot=(0.57735,-0.57735,-0.57735;2.0944rad)
  sketch-geometry (1):
    g0: Circle CenterX=33.9 CenterY=0 CenterZ=0 NormalX=0 NormalY=0 NormalZ=1 AngleXU=0 Radius=1.5
  constraints (2):
    c: DistanceX(g0,g-3) = 6.6
    c: Radius(g0) = 1.5
FEATURE [PartDesign::Pocket] Pocket119
  BaseFeature = -> Pad150
  Direction = (1,0,0)
  Length = 16
  Length2 = 5
  Profile = -> Sketch257
  ReferenceAxis = -> Sketch257 [N_Axis]
  Refine = true
  Suppressed = false
  Type = 0
FEATURE [Sketcher::SketchObject] Sketch258
  ArcFitTolerance = 1e-06
  AttachmentSupport = -> [Pocket119]
  ExternalGeometry = -> [Pocket119]
  FullyConstrained = true
  MakeInternals = false
  MapMode = 5
  Placement = pos=(-6.44,8e-15,0) rot=(-0.57735,0.57735,0.57735;4.18879rad)
  sketch-geometry (1):
    g0: Circle CenterX=44.5 CenterY=0 CenterZ=0 NormalX=0 NormalY=0 NormalZ=1 AngleXU=0 Radius=1.5
  constraints (3):
    c: PointOnObject(g0,g-1)
    c: Radius(g0) = 1.5
    c: DistanceX(g0,g-3) = 2.5
FEATURE [PartDesign::Pocket] Pocket120
  BaseFeature = -> Pocket119
  Direction = (1,-1.3e-15,0)
  Length = 12
  Length2 = 5
  Profile = -> Sketch258
  ReferenceAxis = -> Sketch258 [N_Axis]
  Refine = true
  Suppressed = false
  Type = 0
FEATURE [Sketcher::SketchObject] Sketch259
  ArcFitTolerance = 1e-06
  AttachmentSupport = -> [Pocket120]
  ExternalGeometry = -> [Pocket120]
  FullyConstrained = true
  MakeInternals = false
  MapMode = 5
  sketch-geometry (4):
    g0: LineSegment StartX=-3.84 StartY=0 StartZ=0 EndX=2.26 EndY=0 EndZ=0
    g1: LineSegment StartX=2.26 StartY=0 StartZ=0 EndX=2.26 EndY=3.2 EndZ=0
    g2: LineSegment StartX=2.26 StartY=3.2 StartZ=0 EndX=-3.84 EndY=3.2 EndZ=0
    g3: LineSegment StartX=-3.84 StartY=3.2 StartZ=0 EndX=-3.84 EndY=0 EndZ=0
  constraints (12):
    c: Coincident(g0,g1)
    c: Coincident(g1,g2)
    c: Coincident(g2,g3)
    c: Coincident(g3,g0)
    c: Horizontal(g0)
    c: Horizontal(g2)
    c: Vertical(g1)
    c: Vertical(g3)
    c: PointOnObject(g0,g-1)
    c: DistanceX(g2,g2) = 6.1
    c: DistanceY(g3,g3) = 3.2
    c: DistanceX(g-3,g0) = 5.45
FEATURE [PartDesign::Pad] Pad151
  BaseFeature = -> Pocket120
  Direction = (0,0,1)
  Length = 1.2
  Length2 = 10
  Profile = -> Sketch259
  ReferenceAxis = -> Sketch259 [N_Axis]
  Refine = true
  Suppressed = false
  Type = 0
FEATURE [Sketcher::SketchObject] Sketch260
  ArcFitTolerance = 1e-06
  AttachmentSupport = -> [Pad151]
  ExternalGeometry = -> [Pad151]
  FullyConstrained = false
  MakeInternals = false
  MapMode = 5
  Placement = pos=(0,0,-3) rot=(1,0,0;3.14159rad)
  sketch-geometry (1):
    g0: Circle CenterX=-0.788817 CenterY=25.5 CenterZ=0 NormalX=0 NormalY=0 NormalZ=1 AngleXU=0 Radius=7.5
  constraints (2):
    c: Diameter(g0) = 15
    c: DistanceY(g0,g-3) = 22.5
FEATURE [PartDesign::Pad] Pad152
  BaseFeature = -> Pad151
  Direction = (0,0,-1)
  Length = 1.25
  Length2 = 10
  Profile = -> Sketch260
  ReferenceAxis = -> Sketch260 [N_Axis]
  Refine = true
  Suppressed = false
  Type = 0
FEATURE [Sketcher::SketchObject] Sketch261
  ArcFitTolerance = 1e-06
  AttachmentSupport = -> [Pad152]
  ExternalGeometry = -> [Pad152]
  FullyConstrained = true
  MakeInternals = false
  MapMode = 5
  Placement = pos=(0,0,-4.25) rot=(1,0,0;3.14159rad)
  sketch-geometry (1):
    g0: Circle CenterX=-0.788817 CenterY=25.5 CenterZ=0 NormalX=0 NormalY=0 NormalZ=1 AngleXU=0 Radius=6.5
  constraints (2):
    c: Coincident(g0,g-3)
    c: Diameter(g0) = 13
FEATURE [PartDesign::Pad] Pad153
  BaseFeature = -> Pad152
  Direction = (0,0,-1)
  Length = 2.7
  Length2 = 10
  Profile = -> Sketch261
  ReferenceAxis = -> Sketch261 [N_Axis]
  Refine = true
  Suppressed = false
  Type = 0
FEATURE [Sketcher::SketchObject] Sketch262
  ArcFitTolerance = 1e-06
  AttachmentSupport = -> [Pad153]
  ExternalGeometry = -> [Pad153]
  FullyConstrained = true
  MakeInternals = false
  MapMode = 5
  Placement = pos=(0,0,-3) rot=(1,0,0;3.14159rad)
  sketch-geometry (4):
    g0: LineSegment StartX=-6.44 StartY=42.5 StartZ=0 EndX=-6.44 EndY=28.5 EndZ=0
    g1: LineSegment StartX=-6.44 StartY=28.5 StartZ=0 EndX=4.86 EndY=28.5 EndZ=0
    g2: LineSegment StartX=4.86 StartY=28.5 StartZ=0 EndX=4.86 EndY=42.5 EndZ=0
    g3: LineSegment StartX=4.86 StartY=42.5 StartZ=0 EndX=-6.44 EndY=42.5 EndZ=0
  constraints (12):
    c: Coincident(g0,g1)
    c: Coincident(g1,g2)
    c: Coincident(g2,g3)
    c: Coincident(g3,g0)
    c: Vertical(g0)
    c: Vertical(g2)
    c: Horizontal(g1)
    c: Horizontal(g3)
    c: PointOnObject(g0,g-3)
    c: PointOnObject(g2,g-4)
    c: DistanceY(g-3,g0) = 1
    c: DistanceY(g0,g0) = 14
FEATURE [PartDesign::Pad] Pad154
  BaseFeature = -> Pad153
  Direction = (0,0,-1)
  Length = 2.8
  Length2 = 10
  Profile = -> Sketch262
  ReferenceAxis = -> Sketch262 [N_Axis]
  Refine = true
  Suppressed = false
  Type = 0
FEATURE [Sketcher::SketchObject] Sketch263
  ArcFitTolerance = 1e-06
  AttachmentSupport = -> [Pad154]
  ExternalGeometry = -> [Pad154]
  FullyConstrained = true
  MakeInternals = false
  MapMode = 5
  Placement = pos=(-6.44,0,-5.3e-15) rot=(0.57735,-0.57735,-0.57735;2.0944rad)
  sketch-geometry (3):
    g0: LineSegment StartX=42.5 StartY=-3 StartZ=0 EndX=42.5 EndY=-5.8 EndZ=0
    g1: LineSegment StartX=42.5 StartY=-5.8 StartZ=0 EndX=40.8834 EndY=-5.8 EndZ=0
    g2: LineSegment StartX=42.5 StartY=-3 StartZ=0 EndX=40.8834 EndY=-5.8 EndZ=0
  constraints (7):
    c: Coincident(g0,g-3)
    c: Coincident(g0,g-4)
    c: Coincident(g1,g0)
    c: PointOnObject(g1,g-4)
    c: Coincident(g2,g0)
    c: Coincident(g2,g1)
    c: Angle(g2,g0) = 0.523599
FEATURE [PartDesign::Pocket] Pocket121
  BaseFeature = -> Pad154
  Direction = (1,0,0)
  Length = 12
  Length2 = 5
  Profile = -> Sketch263
  ReferenceAxis = -> Sketch263 [N_Axis]
  Refine = true
  Suppressed = false
  Type = 0
FEATURE [Sketcher::SketchObject] Sketch264
  ArcFitTolerance = 1e-06
  AttachmentSupport = -> [Pocket121]
  ExternalGeometry = -> [Pocket121]
  FullyConstrained = true
  MakeInternals = false
  MapMode = 5
  Placement = pos=(0,0,-6.95) rot=(1,0,0;3.14159rad)
  sketch-geometry (1):
    g0: Circle CenterX=-0.788817 CenterY=25.5 CenterZ=0 NormalX=0 NormalY=0 NormalZ=1 AngleXU=0 Radius=3.875
  constraints (2):
    c: Coincident(g0,g-3)
    c: Diameter(g0) = 7.75
FEATURE [PartDesign::Pocket] Pocket122
  BaseFeature = -> Pocket121
  Direction = (0,0,1)
  Length = 6
  Length2 = 5
  Profile = -> Sketch264
  ReferenceAxis = -> Sketch264 [N_Axis]
  Refine = true
  Suppressed = false
  Type = 0
FEATURE [PartDesign::SubShapeBinder] Binder001
  BindCopyOnChange = 0
  BindMode = 2
  ClaimChildren = false
  Fuse = false
  MakeFace = true
  OffsetFill = false
  OffsetIntersection = false
  OffsetJoinType = 0
  OffsetOpenResult = false
  PartialLoad = false
  Placement = pos=(0,0,1) rot=(0,0,1;0rad)
  Refine = true
  Relative = true
  _Version = 2
FEATURE [Sketcher::SketchObject] Sketch265
  ArcFitTolerance = 1e-06
  AttachmentSupport = -> [Pocket122]
  ExternalGeometry = -> [Binder001]
  FullyConstrained = true
  MakeInternals = false
  MapMode = 5
  Placement = pos=(0,0,-1.5) rot=(0,0,1;0rad)
  sketch-geometry (1):
    g0: Circle CenterX=-24 CenterY=-38.05 CenterZ=0 NormalX=0 NormalY=0 NormalZ=1 AngleXU=0 Radius=0.75
  constraints (2):
    c: Coincident(g0,g-3)
    c: Equal(g0,g-3)
FEATURE [PartDesign::Pocket] Pocket123
  BaseFeature = -> Pocket122
  Direction = (0,0,-1)
  Length = 5
  Length2 = 5
  Profile = -> Sketch265
  ReferenceAxis = -> Sketch265 [N_Axis]
  Refine = true
  Suppressed = false
  Type = 0
FEATURE [Sketcher::SketchObject] Sketch266
  ArcFitTolerance = 1e-06
  AttachmentSupport = -> [Pocket123]
  FullyConstrained = true
  MakeInternals = false
  MapMode = 5
  Placement = pos=(0,0,-1.5) rot=(0,0,1;0rad)
  sketch-geometry (1):
    g0: Circle CenterX=-0.79 CenterY=-37.8 CenterZ=0 NormalX=0 NormalY=0 NormalZ=1 AngleXU=0 Radius=2.25
  constraints (2):
    c: Coincident(g0,g-3)
    c: Diameter(g0) = 4.5
FEATURE [PartDesign::Pocket] Pocket124
  BaseFeature = -> Pocket123
  Direction = (0,0,-1)
  Length = 1
  Length2 = 5
  Profile = -> Sketch266
  ReferenceAxis = -> Sketch266 [N_Axis]
  Refine = true
  Suppressed = false
  Type = 0
FEATURE [Sketcher::SketchObject] Sketch267
  ArcFitTolerance = 1e-06
  AttachmentSupport = -> [Pocket124]
  ExternalGeometry = -> [Pocket124]
  FullyConstrained = true
  MakeInternals = false
  MapMode = 5
  Placement = pos=(0,0,-1.5) rot=(0,0,1;0rad)
  sketch-geometry (1):
    g0: Circle CenterX=-0.788817 CenterY=-25.5 CenterZ=0 NormalX=0 NormalY=0 NormalZ=1 AngleXU=0 Radius=5
  constraints (2):
    c: Coincident(g0,g-3)
    c: Diameter(g0) = 10
FEATURE [PartDesign::Pocket] Pocket125
  BaseFeature = -> Pocket124
  Direction = (0,0,-1)
  Length = 3.9
  Length2 = 5
  Profile = -> Sketch267
  ReferenceAxis = -> Sketch267 [N_Axis]
  Refine = true
  Suppressed = false
  Type = 0
FEATURE [Sketcher::SketchObject] Sketch268
  ArcFitTolerance = 1e-06
  AttachmentSupport = -> [Pocket125]
  ExternalGeometry = -> [Pocket125]
  FullyConstrained = true
  MakeInternals = false
  MapMode = 5
  Placement = pos=(0,0,-1.5) rot=(0,0,1;0rad)
  sketch-geometry (1):
    g0: Circle CenterX=-0.788817 CenterY=-25.5 CenterZ=0 NormalX=0 NormalY=0 NormalZ=1 AngleXU=0 Radius=6
  constraints (2):
    c: Coincident(g0,g-3)
    c: Diameter(g0) = 12
FEATURE [PartDesign::Pocket] Pocket126
  BaseFeature = -> Pocket125
  Direction = (0,0,-1)
  Length = 1.5
  Length2 = 5
  Profile = -> Sketch268
  ReferenceAxis = -> Sketch268 [N_Axis]
  Refine = true
  Suppressed = false
  Type = 0
FEATURE [Sketcher::SketchObject] Sketch269
  ArcFitTolerance = 1e-06
  AttachmentSupport = -> [Pocket126]
  ExternalGeometry = -> [Pocket126]
  FullyConstrained = true
  MakeInternals = false
  MapMode = 5
  Placement = pos=(0,0,-1.5) rot=(0,0,1;0rad)
  sketch-geometry (6):
    g0: LineSegment StartX=-4.94 StartY=-41.5 StartZ=0 EndX=-4.94 EndY=-31.7464 EndZ=0
    g1: ArcOfCircle CenterX=-0.79 CenterY=-37.8 CenterZ=0 NormalX=0 NormalY=0 NormalZ=1 AngleXU=0 Radius=3.5 StartAngle=1.57046 EndAngle=4.71239
    g2: LineSegment StartX=-0.788817 StartY=-34.3 StartZ=0 EndX=-0.788817 EndY=-33 EndZ=0
    g3: LineSegment StartX=-4.94 StartY=-41.5 StartZ=0 EndX=-0.79 EndY=-41.5 EndZ=0
    g4: LineSegment StartX=-0.79 StartY=-41.3 StartZ=0 EndX=-0.79 EndY=-41.5 EndZ=0
    g5: ArcOfCircle CenterX=-0.788817 CenterY=-25.5 CenterZ=0 NormalX=0 NormalY=0 NormalZ=1 AngleXU=0 Radius=7.5 StartAngle=4.12584 EndAngle=4.71239
  constraints (17):
    c: Vertical(g0)
    c: Coincident(g1,g-3)
    c: Diameter(g1) = 7
    c: Coincident(g2,g1)
    c: Vertical(g2)
    c: Coincident(g3,g0)
    c: Horizontal(g3)
    c: Coincident(g4,g1)
    c: Vertical(g4)
    c: Coincident(g0,g-5)
    c: Coincident(g4,g3)
    c: DistanceX(g1,g1) = 0
    c: Coincident(g5,g2)
    c: Coincident(g5,g-4)
    c: Coincident(g0,g5)
    c: Radius(g5) = 7.5
    c: DistanceX(g2,g5) = 0
FEATURE [PartDesign::Pocket] Pocket127
  BaseFeature = -> Pocket126
  Direction = (0,0,-1)
  Length = 3
  Length2 = 5
  Profile = -> Sketch269
  ReferenceAxis = -> Sketch269 [N_Axis]
  Refine = true
  Suppressed = false
  Type = 0
FEATURE [Sketcher::SketchObject] Sketch270
  ArcFitTolerance = 1e-06
  AttachmentSupport = -> [Pocket127]
  ExternalGeometry = -> [Pocket127]
  FullyConstrained = true
  MakeInternals = false
  MapMode = 5
  Placement = pos=(0,0,-1.5) rot=(0,0,1;0rad)
  sketch-geometry (6):
    g0: ArcOfCircle CenterX=-0.788817 CenterY=-25.5 CenterZ=0 NormalX=0 NormalY=0 NormalZ=1 AngleXU=0 Radius=7.5 StartAngle=4.71239 EndAngle=5.29856
    g1: LineSegment StartX=-0.79 StartY=-41.5 StartZ=0 EndX=-0.79 EndY=-41.3 EndZ=0
    g2: LineSegment StartX=-0.79 StartY=-41.5 StartZ=0 EndX=3.36 EndY=-41.5 EndZ=0
    g3: LineSegment StartX=3.36 StartY=-41.5 StartZ=0 EndX=3.36 EndY=-31.748 EndZ=0
    g4: LineSegment StartX=-0.788817 StartY=-34.3 StartZ=0 EndX=-0.788817 EndY=-33 EndZ=0
    g5: ArcOfCircle CenterX=-0.788817 CenterY=-37.8 CenterZ=0 NormalX=0 NormalY=0 NormalZ=1 AngleXU=0 Radius=3.5 StartAngle=4.71205 EndAngle=7.85398
  constraints (14):
    c: Coincident(g1,g-7)
    c: Coincident(g1,g-7)
    c: Coincident(g2,g1)
    c: Coincident(g2,g-6)
    c: Coincident(g3,g2)
    c: Coincident(g3,g0)
    c: Vertical(g3)
    c: Coincident(g0,g-3)
    c: Coincident(g0,g-4)
    c: Coincident(g4,g-3)
    c: Coincident(g4,g0)
    c: Coincident(g5,g4)
    c: Coincident(g5,g1)
    c: Radius(g5) = 3.5
FEATURE [PartDesign::Pocket] Pocket128
  BaseFeature = -> Pocket127
  Direction = (0,0,-1)
  Length = 3
  Length2 = 5
  Profile = -> Sketch270
  ReferenceAxis = -> Sketch270 [N_Axis]
  Refine = true
  Suppressed = false
  Type = 0
FEATURE [Sketcher::SketchObject] Sketch271
  ArcFitTolerance = 1e-06
  AttachmentSupport = -> [Pocket128]
  ExternalGeometry = -> [Pocket128]
  FullyConstrained = true
  MakeInternals = false
  MapMode = 5
  Placement = pos=(0,0,-1.5) rot=(0,0,1;0rad)
  sketch-geometry (1):
    g0: Circle CenterX=-0.79 CenterY=-4 CenterZ=0 NormalX=0 NormalY=0 NormalZ=1 AngleXU=0 Radius=0.875
  constraints (5):
    c: DistanceY(g-4) = 2.80835e-10
    c: DistanceY(g0,g-3) = 4
    c: Diameter(g0) = 1.75
    c: DistanceX(g-4,g-4) = 5.45
    c: DistanceX(g0,g-4) = 8.5
FEATURE [Sketcher::SketchObject] Sketch272
  ArcFitTolerance = 1e-06
  AttachmentSupport = -> [Pocket128]
  ExternalGeometry = -> [Pocket128]
  FullyConstrained = true
  MakeInternals = false
  MapMode = 5
  Placement = pos=(0,0,-3) rot=(1,0,0;3.14159rad)
  sketch-geometry (1):
    g0: Circle CenterX=-0.79 CenterY=4 CenterZ=0 NormalX=0 NormalY=0 NormalZ=1 AngleXU=0 Radius=2.7
  constraints (3):
    c: Diameter(g0) = 5.4
    c: DistanceY(g-3,g0) = 5.5
    c: DistanceX(g0,g-3) = 10
FEATURE [PartDesign::Pad] Pad155
  BaseFeature = -> Pocket128
  Direction = (0,0,-1)
  Length = 6.3
  Length2 = 10
  Profile = -> Sketch272
  ReferenceAxis = -> Sketch272 [N_Axis]
  Refine = true
  Suppressed = false
  Type = 0
FEATURE [PartDesign::Pocket] Pocket129
  BaseFeature = -> Pad155
  Direction = (0,0,-1)
  Length = 6
  Length2 = 5
  Profile = -> Sketch271
  ReferenceAxis = -> Sketch271 [N_Axis]
  Refine = true
  Suppressed = false
  Type = 0
FEATURE [Sketcher::SketchObject] Sketch273
  ArcFitTolerance = 1e-06
  AttachmentSupport = -> [Pocket129]
  ExternalGeometry = -> [Pocket129]
  FullyConstrained = true
  MakeInternals = false
  MapMode = 5
  Placement = pos=(0,0,-3) rot=(1,0,0;3.14159rad)
  sketch-geometry (8):
    g0: LineSegment StartX=-8.29 StartY=14.7 StartZ=0 EndX=6.71 EndY=14.7 EndZ=0
    g1: LineSegment StartX=-8.29 StartY=6.7 StartZ=0 EndX=6.71 EndY=6.7 EndZ=0
    g2: ArcOfCircle CenterX=-8.29 CenterY=13.7 CenterZ=0 NormalX=0 NormalY=0 NormalZ=1 AngleXU=0 Radius=1 StartAngle=1.5708 EndAngle=3.14159
    g3: ArcOfCircle CenterX=-8.29 CenterY=7.7 CenterZ=0 NormalX=0 NormalY=0 NormalZ=1 AngleXU=0 Radius=1 StartAngle=3.14159 EndAngle=4.71239
    g4: ArcOfCircle CenterX=6.71 CenterY=13.7 CenterZ=0 NormalX=0 NormalY=0 NormalZ=1 AngleXU=0 Radius=1 StartAngle=-9e-16 EndAngle=1.5708
    g5: ArcOfCircle CenterX=6.71 CenterY=7.7 CenterZ=0 NormalX=0 NormalY=0 NormalZ=1 AngleXU=0 Radius=1 StartAngle=4.71239 EndAngle=6.28319
    g6: LineSegment StartX=7.71 StartY=13.7 StartZ=0 EndX=7.71 EndY=7.7 EndZ=0
    g7: LineSegment StartX=-9.29 StartY=13.7 StartZ=0 EndX=-9.29 EndY=7.7 EndZ=0
  constraints (28):
    c: Horizontal(g0)
    c: Horizontal(g1)
    c: Coincident(g2,g0)
    c: Coincident(g3,g1)
    c: Coincident(g4,g0)
    c: Coincident(g5,g1)
    c: Coincident(g6,g4)
    c: Coincident(g6,g5)
    c: Vertical(g6)
    c: Coincident(g7,g2)
    c: Coincident(g7,g3)
    c: Vertical(g7)
    c: DistanceY(g1,g0) = 8
    c: DistanceX(g2,g4) = 17
    c: DistanceX(g-3,g3) = 1.5
    c: Radius(g3) = 1
    c: Radius(g2) = 1
    c: Radius(g4) = 1
    c: Radius(g5) = 1
    c: DistanceY(g-4,g1) = 8.2
    c: DistanceX(g1,g5) = 0
    c: DistanceX(g1,g3) = 0
    c: DistanceX(g2,g0) = 0
    c: DistanceX(g0,g4) = 0
    c: DistanceY(g4,g4) = 0
    c: DistanceY(g5,g5) = 0
    c: DistanceY(g3,g3) = 0
    c: DistanceY(g2,g2) = 0
FEATURE [PartDesign::Pad] Pad156
  BaseFeature = -> Pocket129
  Direction = (0,0,-1)
  Length = 0.1
  Length2 = 10
  Profile = -> Sketch273
  ReferenceAxis = -> Sketch273 [N_Axis]
  Refine = true
  Suppressed = false
  Type = 0
FEATURE [Sketcher::SketchObject] Sketch274
  ArcFitTolerance = 1e-06
  AttachmentSupport = -> [Pad156]
  ExternalGeometry = -> [Pad156]
  FullyConstrained = true
  MakeInternals = false
  MapMode = 5
  Placement = pos=(0,0,-3.1) rot=(1,0,0;3.14159rad)
  sketch-geometry (8):
    g0: ArcOfCircle CenterX=-7.79 CenterY=13.2 CenterZ=0 NormalX=0 NormalY=0 NormalZ=1 AngleXU=0 Radius=1 StartAngle=1.5708 EndAngle=3.14159
    g1: ArcOfCircle CenterX=6.21 CenterY=13.2 CenterZ=0 NormalX=0 NormalY=0 NormalZ=1 AngleXU=0 Radius=1 StartAngle=2e-16 EndAngle=1.5708
    g2: ArcOfCircle CenterX=6.21 CenterY=9.7 CenterZ=0 NormalX=0 NormalY=0 NormalZ=1 AngleXU=0 Radius=1 StartAngle=4.71239 EndAngle=6.28319
    g3: ArcOfCircle CenterX=-7.79 CenterY=9.7 CenterZ=0 NormalX=0 NormalY=0 NormalZ=1 AngleXU=0 Radius=1 StartAngle=3.14159 EndAngle=4.71239
    g4: LineSegment StartX=-8.79 StartY=13.2 StartZ=0 EndX=-8.79 EndY=9.7 EndZ=0
    g5: LineSegment StartX=-7.79 StartY=14.2 StartZ=0 EndX=6.21 EndY=14.2 EndZ=0
    g6: LineSegment StartX=7.21 StartY=13.2 StartZ=0 EndX=7.21 EndY=9.7 EndZ=0
    g7: LineSegment StartX=6.21 StartY=8.7 StartZ=0 EndX=-7.79 EndY=8.7 EndZ=0
  constraints (28):
    c: Coincident(g4,g0)
    c: Coincident(g4,g3)
    c: Vertical(g4)
    c: Coincident(g5,g0)
    c: Coincident(g5,g1)
    c: Horizontal(g5)
    c: Coincident(g6,g1)
    c: Coincident(g6,g2)
    c: Vertical(g6)
    c: Coincident(g7,g2)
    c: Coincident(g7,g3)
    c: Horizontal(g7)
    c: DistanceY(g-3,g3) = 2
    c: DistanceX(g-4,g0) = 0.5
    c: DistanceY(g0,g-5) = 0.5
    c: Radius(g3) = 1
    c: Radius(g0) = 1
    c: Radius(g1) = 1
    c: Radius(g2) = 1
    c: DistanceX(g0,g0) = 0
    c: DistanceX(g1,g1) = 0
    c: DistanceX(g2,g2) = 0
    c: DistanceX(g3,g3) = 0
    c: DistanceY(g3,g3) = 0
    c: DistanceY(g0,g0) = 0
    c: DistanceY(g1,g1) = 0
    c: DistanceY(g2,g2) = 0
    c: DistanceX(g1,g-6) = 0.5
FEATURE [PartDesign::Pad] Pad157
  BaseFeature = -> Pad156
  Direction = (0,0,-1)
  Length = 0.1
  Length2 = 10
  Profile = -> Sketch274
  ReferenceAxis = -> Sketch274 [N_Axis]
  Refine = true
  Suppressed = false
  Type = 0
FEATURE [PartDesign::Fillet] Fillet048
  Base = -> Pad157 [Edge162]
  BaseFeature = -> Pad157
  Radius = 1
  Refine = true
  SupportTransform = false
  Suppressed = false
  UseAllEdges = false
FEATURE [PartDesign::Body] Body022  label="Rear_Torso"
  AllowCompound = false
  Group = -> [Sketch254,Pad149,Sketch255,Pad150,Sketch257,Pocket119,Sketch258,Pocket120,Sketch259,Pad151,Sketch260,Pad152,Sketch261,Pad153,Sketch262,Pad154,Sketch263,Pocket121,Sketch264,Pocket122,Binder001,Sketch265,Pocket123,Sketch266,Pocket124,Sketch267,Pocket125,Sketch268,Pocket126,Sketch269,Pocket127,Sketch270,Pocket128,Sketch271,Sketch272,Pad155,Pocket129,Sketch273,Pad156,Sketch274,Pad157,Fillet048,+26 more]
  Origin = -> Origin024
  Placement = pos=(39,-6.5,0) rot=(0,0,1;0rad)
  Tip = -> Pocket168
COMPONENT P12 — recipe-attached ("Devastator_Arm_Joint", modeled in this document).
Construction recipe (the document's own serialized feature program — sketch geometry with constraints, then the solid features built on it; lengths are millimeters unless a unit is written):

FEATURE [Sketcher::SketchObject] Sketch275
  ArcFitTolerance = 1e-06
  AttachmentSupport = -> [XY_Plane025]
  FullyConstrained = true
  MakeInternals = false
  MapMode = 5
  sketch-geometry (1):
    g0: Circle CenterX=0 CenterY=0 CenterZ=0 NormalX=0 NormalY=0 NormalZ=1 AngleXU=0 Radius=3.75
  constraints (2):
    c: Coincident(g0,g-1)
    c: Diameter(g0) = 7.5
FEATURE [PartDesign::Pad] Pad158
  Direction = (0,0,1)
  Length = 10
  Length2 = 10
  Profile = -> Sketch275
  ReferenceAxis = -> Sketch275 [N_Axis]
  Refine = true
  Suppressed = false
  Type = 0
FEATURE [Sketcher::SketchObject] Sketch276
  ArcFitTolerance = 1e-06
  AttachmentSupport = -> [Pad158]
  FullyConstrained = true
  MakeInternals = false
  MapMode = 5
  Placement = pos=(0,0,10) rot=(0,0,1;0rad)
  sketch-geometry (1):
    g0: Circle CenterX=0 CenterY=0 CenterZ=0 NormalX=0 NormalY=0 NormalZ=1 AngleXU=0 Radius=5.75
  constraints (2):
    c: Coincident(g0,g-1)
    c: Diameter(g0) = 11.5
FEATURE [PartDesign::Pad] Pad159
  BaseFeature = -> Pad158
  Direction = (0,0,1)
  Length = 2.5
  Length2 = 10
  Profile = -> Sketch276
  ReferenceAxis = -> Sketch276 [N_Axis]
  Refine = true
  Suppressed = false
  Type = 0
FEATURE [Sketcher::SketchObject] Sketch277
  ArcFitTolerance = 1e-06
  AttachmentSupport = -> [Pad159]
  FullyConstrained = true
  MakeInternals = false
  MapMode = 5
  Placement = pos=(0,0,12.5) rot=(0,0,1;0rad)
  sketch-geometry (1):
    g0: Circle CenterX=0 CenterY=0 CenterZ=0 NormalX=0 NormalY=0 NormalZ=1 AngleXU=0 Radius=2.95
  constraints (2):
    c: Coincident(g0,g-1)
    c: Diameter(g0) = 5.9
FEATURE [PartDesign::Pocket] Pocket130
  BaseFeature = -> Pad159
  Direction = (0,0,-1)
  Length = 1.1
  Length2 = 5
  Profile = -> Sketch277
  ReferenceAxis = -> Sketch277 [N_Axis]
  Refine = true
  Suppressed = false
  Type = 0
FEATURE [Sketcher::SketchObject] Sketch278
  ArcFitTolerance = 1e-06
  AttachmentSupport = -> [Pocket130]
  FullyConstrained = true
  MakeInternals = false
  MapMode = 5
  Placement = pos=(0,0,11.4) rot=(0,0,1;0rad)
  sketch-geometry (1):
    g0: Circle CenterX=0 CenterY=0 CenterZ=0 NormalX=0 NormalY=0 NormalZ=1 AngleXU=0 Radius=2.45
  constraints (2):
    c: Coincident(g0,g-1)
    c: Diameter(g0) = 4.9
FEATURE [PartDesign::Pocket] Pocket131
  BaseFeature = -> Pocket130
  Direction = (0,0,-1)
  Length = 3.6
  Length2 = 5
  Profile = -> Sketch278
  ReferenceAxis = -> Sketch278 [N_Axis]
  Refine = true
  Suppressed = false
  Type = 0
FEATURE [Sketcher::SketchObject] Sketch279
  ArcFitTolerance = 1e-06
  AttachmentSupport = -> [Pocket131]
  ExternalGeometry = -> [Pocket131]
  FullyConstrained = true
  MakeInternals = false
  MapMode = 5
  Placement = pos=(0,0,12.5) rot=(0,0,1;0rad)
  sketch-geometry (24):
    g0: LineSegment StartX=-0.5 StartY=6.25 StartZ=0 EndX=-0.5 EndY=1.25 EndZ=0
    g1: LineSegment StartX=-0.5 StartY=1.25 StartZ=0 EndX=-4.03553 EndY=4.78553 EndZ=0
    g2: LineSegment StartX=-1.16421 StartY=0.5 StartZ=0 EndX=-4.74264 EndY=4.07843 EndZ=0
    g3: LineSegment StartX=-1.16421 StartY=0.5 StartZ=0 EndX=-6.16421 EndY=0.5 EndZ=0
    g4: LineSegment StartX=6.16421 StartY=-0.5 StartZ=0 EndX=1.16421 EndY=-0.5 EndZ=0
    g5: LineSegment StartX=1.16421 StartY=-0.5 StartZ=0 EndX=4.69975 EndY=-4.03553 EndZ=0
    g6: LineSegment StartX=3.99264 StartY=-4.74264 StartZ=0 EndX=0.5 EndY=-1.25 EndZ=0
    g7: LineSegment StartX=0.5 StartY=-1.25 StartZ=0 EndX=0.5 EndY=-6.25 EndZ=0
    g8: LineSegment StartX=-0.5 StartY=-6.25 StartZ=0 EndX=-0.5 EndY=-1.25 EndZ=0
    g9: LineSegment StartX=-0.5 StartY=-1.25 StartZ=0 EndX=-3.99264 EndY=-4.74264 EndZ=0
    g10: LineSegment StartX=-6.16421 StartY=-0.5 StartZ=0 EndX=-1.16421 EndY=-0.5 EndZ=0
    g11: LineSegment StartX=-1.16421 StartY=-0.5 StartZ=0 EndX=-4.69975 EndY=-4.03553 EndZ=0
    g12: LineSegment StartX=0.5 StartY=6.25 StartZ=0 EndX=0.5 EndY=1.25 EndZ=0
    g13: LineSegment StartX=0.5 StartY=1.25 StartZ=0 EndX=4.03553 EndY=4.78553 EndZ=0
    g14: LineSegment StartX=6.16421 StartY=0.5 StartZ=0 EndX=1.16421 EndY=0.5 EndZ=0
    g15: LineSegment StartX=1.16421 StartY=0.5 StartZ=0 EndX=4.74264 EndY=4.07843 EndZ=0
    g16: LineSegment StartX=-4.03553 StartY=4.78553 StartZ=0 EndX=-4.74264 EndY=4.07843 EndZ=0
    g17: LineSegment StartX=-0.5 StartY=6.25 StartZ=0 EndX=0.5 EndY=6.25 EndZ=0
    g18: LineSegment StartX=4.03553 StartY=4.78553 StartZ=0 EndX=4.74264 EndY=4.07843 EndZ=0
    g19: LineSegment StartX=6.16421 StartY=0.5 StartZ=0 EndX=6.16421 EndY=-0.5 EndZ=0
    g20: LineSegment StartX=4.69975 StartY=-4.03553 StartZ=0 EndX=3.99264 EndY=-4.74264 EndZ=0
    g21: LineSegment StartX=0.5 StartY=-6.25 StartZ=0 EndX=-0.5 EndY=-6.25 EndZ=0
    g22: LineSegment StartX=-3.99264 StartY=-4.74264 StartZ=0 EndX=-4.69975 EndY=-4.03553 EndZ=0
    g23: LineSegment StartX=-6.16421 StartY=-0.5 StartZ=0 EndX=-6.16421 EndY=0.5 EndZ=0
  constraints (72):
    c: Vertical(g0)
    c: Coincident(g1,g0)
    c: Coincident(g3,g2)
    c: Horizontal(g3)
    c: Horizontal(g4)
    c: Coincident(g5,g4)
    c: Coincident(g7,g6)
    c: Vertical(g7)
    c: Vertical(g8)
    c: Coincident(g9,g8)
    c: Horizontal(g10)
    c: Coincident(g11,g10)
    c: Vertical(g12)
    c: Coincident(g13,g12)
    c: Horizontal(g14)
    c: Coincident(g15,g14)
    c: Coincident(g16,g1)
    c: Coincident(g16,g2)
    c: Coincident(g17,g0)
    c: Coincident(g17,g12)
    c: Coincident(g18,g13)
    c: Coincident(g18,g15)
    c: Coincident(g19,g14)
    c: Coincident(g19,g4)
    c: Coincident(g20,g5)
    c: Coincident(g20,g6)
    c: Coincident(g21,g7)
    c: Coincident(g21,g8)
    c: Coincident(g22,g9)
    c: Coincident(g22,g11)
    c: Coincident(g23,g10)
    c: Coincident(g23,g3)
    c: Vertical(g23)
    c: DistanceX(g17,g17) = 1
    c: DistanceX(g21,g21) = 1
    c: DistanceY(g23,g23) = 1
    c: DistanceY(g19,g19) = 1
    c: Distance(g18) = 1
    c: Distance(g22) = 1
    c: Angle(g10,g11) = 0.785398
    c: Angle(g9,g8) = 0.785398
    c: Angle(g7,g6) = 0.785398
    c: Angle(g5,g4) = 0.785398
    c: Angle(g14,g15) = 0.785398
    c: Angle(g13,g12) = 0.785398
    c: Angle(g0,g1) = 0.785398
    c: Angle(g2,g3) = 0.785398
    c: Horizontal(g17)
    c: Horizontal(g21)
    c: Vertical(g19)
    c: Distance(g20) = 1
    c: Distance(g16) = 1
    c: Angle(g13,g18) = 1.5708
    c: Angle(g16,g1) = 1.5708
    c: Angle(g22,g11) = 1.5708
    c: Angle(g5,g20) = 1.5708
    c: DistanceX(g0,g-1) = 0.5
    c: DistanceX(g-1,g6) = 0.5
    c: DistanceY(g-1,g14) = 0.5
    c: DistanceY(g-1,g2) = 0.5
    c: DistanceX(g3,g3) = 5
    c: DistanceX(g14,g14) = 5
    c: DistanceY(g0,g0) = 5
    c: DistanceY(g8,g8) = 5
    c: Distance(g13) = 5
    c: Distance(g5) = 5
    c: Distance(g11) = 5
    c: Distance(g1) = 5
    c: DistanceY(g12,g0) = 0
    c: DistanceY(g8,g6) = 0
    c: DistanceX(g2,g10) = 0
    c: DistanceY(g8,g0) = 2.5
FEATURE [PartDesign::Pocket] Pocket132
  BaseFeature = -> Pocket131
  Direction = (0,0,-1)
  Length = 1
  Length2 = 5
  Profile = -> Sketch279
  ReferenceAxis = -> Sketch279 [N_Axis]
  Refine = true
  Suppressed = false
  Type = 0
FEATURE [PartDesign::Chamfer] Chamfer
  Angle = 45
  Base = -> Pocket132 [Edge91,Edge85,Edge83,Edge77,Edge75,Edge69,Edge67,Edge61,Edge59,Edge53,Edge51,Edge45,Edge43,Edge101,Edge99,Edge93]
  BaseFeature = -> Pocket132
  ChamferType = 0
  FlipDirection = false
  Refine = true
  Size = 0.5
  Size2 = 1
  SupportTransform = false
  Suppressed = false
  UseAllEdges = false
FEATURE [Sketcher::SketchObject] Sketch280
  ArcFitTolerance = 1e-06
  AttachmentSupport = -> [Chamfer]
  FullyConstrained = true
  MakeInternals = false
  MapMode = 5
  Placement = pos=(0,0,0) rot=(1,0,0;3.14159rad)
  sketch-geometry (4):
    g0: LineSegment StartX=-2 StartY=2 StartZ=0 EndX=-2 EndY=-2 EndZ=0
    g1: LineSegment StartX=-2 StartY=-2 StartZ=0 EndX=2 EndY=-2 EndZ=0
    g2: LineSegment StartX=2 StartY=-2 StartZ=0 EndX=2 EndY=2 EndZ=0
    g3: LineSegment StartX=2 StartY=2 StartZ=0 EndX=-2 EndY=2 EndZ=0
  constraints (12):
    c: Coincident(g0,g1)
    c: Coincident(g1,g2)
    c: Coincident(g2,g3)
    c: Coincident(g3,g0)
    c: Vertical(g0)
    c: Vertical(g2)
    c: Horizontal(g1)
    c: Horizontal(g3)
    c: DistanceX(g0,g-1) = 2
    c: DistanceX(g-1,g2) = 2
    c: DistanceY(g-1,g2) = 2
    c: DistanceY(g1,g-1) = 2
FEATURE [PartDesign::Pocket] Pocket133
  BaseFeature = -> Chamfer
  Direction = (0,0,1)
  Length = 6.25
  Length2 = 5
  Profile = -> Sketch280
  ReferenceAxis = -> Sketch280 [N_Axis]
  Refine = true
  Suppressed = false
  Type = 0
FEATURE [PartDesign::Body] Body023  label="Devastator_Arm_Joint"
  AllowCompound = false
  Group = -> [Sketch275,Pad158,Sketch276,Pad159,Sketch277,Pocket130,Sketch278,Pocket131,Sketch279,Pocket132,Chamfer,Sketch280,Pocket133]
  Origin = -> Origin025
  Placement = pos=(38.2,-32,-11) rot=(0,0,1;3.14159rad)
  Tip = -> Pocket133
